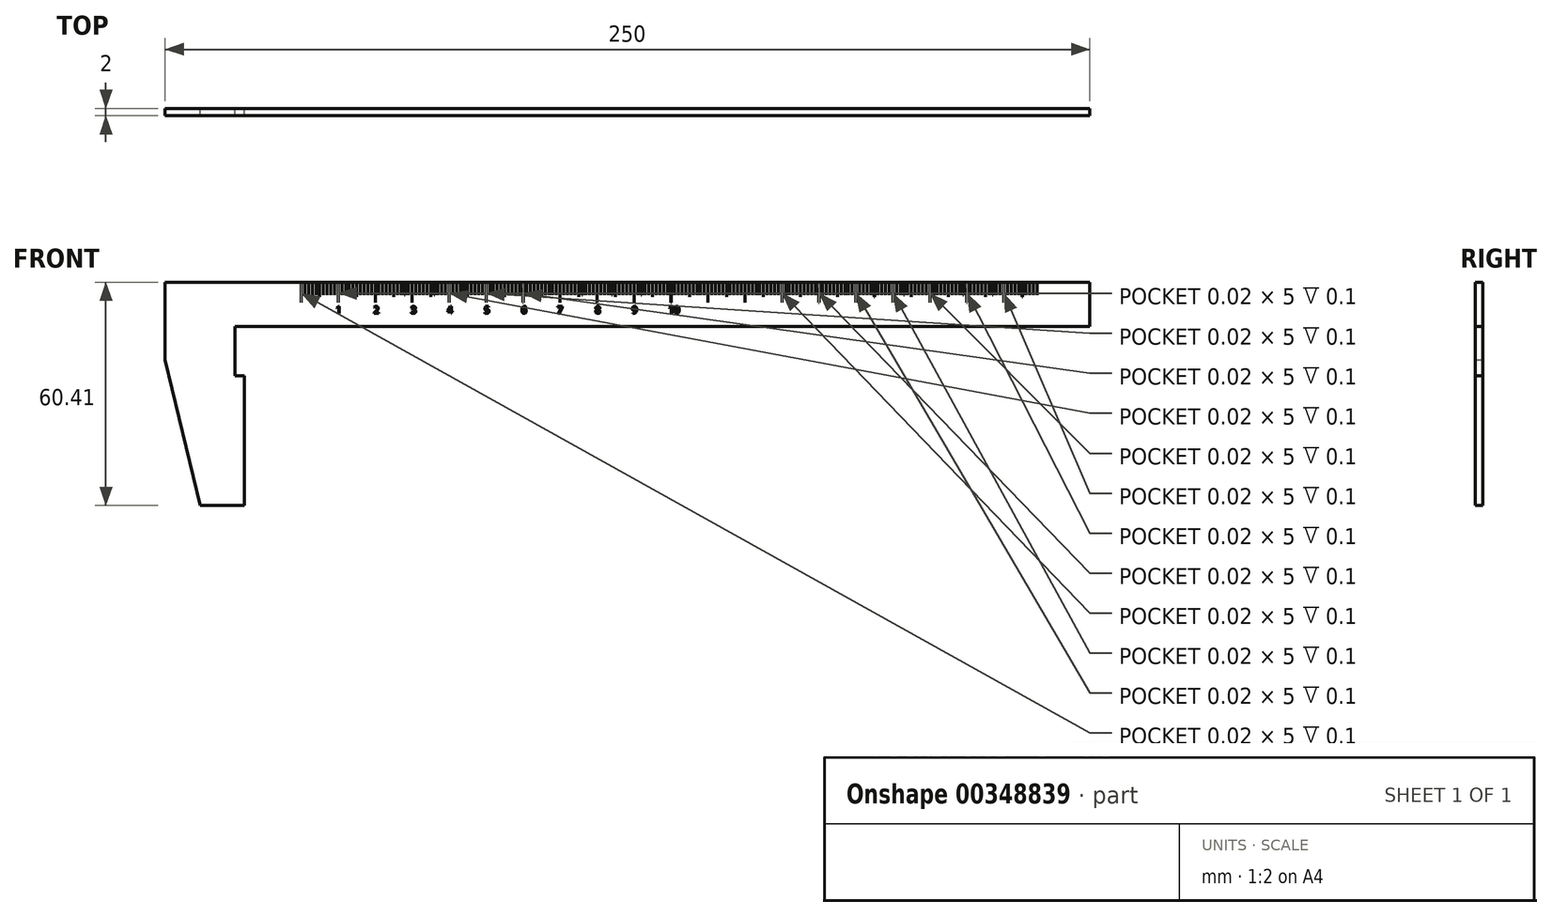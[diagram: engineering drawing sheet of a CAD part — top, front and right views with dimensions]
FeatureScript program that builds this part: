
annotation { "Feature Type Name" : "Feature", "Feature Type Description" : "" }
export const myFeature = defineFeature(function(context is Context, id is Id, definition is map)
    precondition{}
    {
        {
            var Q0;
            Q0=qCreatedBy(makeId("Front.planeOp"),FACE);
            var sketch = newSketch(context, id + "F0", { "sketchPlane" : qUnion([Q0])});
            skLineSegment(sketch, "E0.bottom", {"start": v(-86.98, 12) * mm, "end": v(123.02, 12) * mm});
            skLineSegment(sketch, "E0.top", {"start": v(-86.98, 0) * mm, "end": v(123.02, 0) * mm});
            skLineSegment(sketch, "E0.left", {"start": v(-86.98, 12) * mm, "end": v(-86.98, 0) * mm});
            skLineSegment(sketch, "E0.right", {"start": v(123.02, 12) * mm, "end": v(123.02, 0) * mm});
            skLineSegment(sketch, "E1", {"start": v(-86.98, 12) * mm, "end": v(-126.98, 12) * mm});
            skLineSegment(sketch, "E2", {"start": v(-126.98, 12) * mm, "end": v(-126.98, -9.03) * mm});
            skLineSegment(sketch, "E3", {"start": v(-126.98, -9.03) * mm, "end": v(-117.52, -48.4) * mm});
            skLineSegment(sketch, "E4", {"start": v(-105.6, -48.4) * mm, "end": v(-105.6, -13.34) * mm});
            skLineSegment(sketch, "E5", {"start": v(-105.6, 0) * mm, "end": v(-86.98, 0) * mm});
            skLineSegment(sketch, "E6", {"start": v(-117.52, -48.4) * mm, "end": v(-105.6, -48.4) * mm});
            skLineSegment(sketch, "E7", {"start": v(-105.6, -13.34) * mm, "end": v(-108.05, -13.33) * mm});
            skLineSegment(sketch, "E8", {"start": v(-108.05, -13.33) * mm, "end": v(-108.05, 0) * mm});
            skLineSegment(sketch, "E9", {"start": v(-108.05, 0) * mm, "end": v(-105.6, 0) * mm});
            skSolve(sketch);
        }
        {
            var Q0;
            Q0 = qSketchRegion(id + "F0", true);
            extrude(context, id + "F1", {"entities" : qUnion([Q0]), "depth" : 2 * mm});
        }
        {
            var Q0;
            Q0=makeQuery(id+"F1.opExtrude","CAP_FACE",FACE,{"disambiguationData":[OSD([sQuery(id+"F0.wireOp",EDGE,"E0.bottom"),sQuery(id+"F0.wireOp",EDGE,"E0.top"),sQuery(id+"F0.wireOp",EDGE,"E0.left"),sQuery(id+"F0.wireOp",EDGE,"E0.right")])],"isStart":false});
            var sketch = newSketch(context, id + "F2", { "sketchPlane" : qUnion([Q0])});
            skLineSegment(sketch, "E10.bottom", {"start": v(-90.2, 11.5) * mm, "end": v(-90.18, 11.5) * mm});
            skLineSegment(sketch, "E10.top", {"start": v(-90.2, 6.5) * mm, "end": v(-90.18, 6.5) * mm});
            skLineSegment(sketch, "E10.left", {"start": v(-90.2, 11.5) * mm, "end": v(-90.2, 6.5) * mm});
            skLineSegment(sketch, "E10.right", {"start": v(-90.18, 11.5) * mm, "end": v(-90.18, 6.5) * mm});
            skLineSegment(sketch, "E11.bottom", {"start": v(-89.2, 11.5) * mm, "end": v(-89.19, 11.5) * mm});
            skLineSegment(sketch, "E11.top", {"start": v(-89.2, 8.5) * mm, "end": v(-89.19, 8.5) * mm});
            skLineSegment(sketch, "E11.left", {"start": v(-89.2, 11.5) * mm, "end": v(-89.2, 8.5) * mm});
            skLineSegment(sketch, "E11.right", {"start": v(-89.19, 11.5) * mm, "end": v(-89.19, 8.5) * mm});
            skLineSegment(sketch, "E12.1.0.0", {"start": v(-88.2, 11.5) * mm, "end": v(-88.2, 8.5) * mm});
            skLineSegment(sketch, "E12.1.0.1", {"start": v(-88.19, 11.5) * mm, "end": v(-88.19, 8.5) * mm});
            skLineSegment(sketch, "E12.1.0.2", {"start": v(-88.2, 11.5) * mm, "end": v(-88.19, 11.5) * mm});
            skLineSegment(sketch, "E12.1.0.3", {"start": v(-88.2, 8.5) * mm, "end": v(-88.19, 8.5) * mm});
            skLineSegment(sketch, "E12.2.0.0", {"start": v(-87.2, 11.5) * mm, "end": v(-87.2, 8.5) * mm});
            skLineSegment(sketch, "E12.2.0.1", {"start": v(-87.19, 11.5) * mm, "end": v(-87.19, 8.5) * mm});
            skLineSegment(sketch, "E12.2.0.2", {"start": v(-87.2, 11.5) * mm, "end": v(-87.19, 11.5) * mm});
            skLineSegment(sketch, "E12.2.0.3", {"start": v(-87.2, 8.5) * mm, "end": v(-87.19, 8.5) * mm});
            skLineSegment(sketch, "E12.3.0.0", {"start": v(-86.2, 11.5) * mm, "end": v(-86.2, 8.5) * mm});
            skLineSegment(sketch, "E12.3.0.1", {"start": v(-86.19, 11.5) * mm, "end": v(-86.19, 8.5) * mm});
            skLineSegment(sketch, "E12.3.0.2", {"start": v(-86.2, 11.5) * mm, "end": v(-86.19, 11.5) * mm});
            skLineSegment(sketch, "E12.3.0.3", {"start": v(-86.2, 8.5) * mm, "end": v(-86.19, 8.5) * mm});
            skLineSegment(sketch, "E12.5.0.0", {"start": v(-84.2, 11.5) * mm, "end": v(-84.2, 8.5) * mm});
            skLineSegment(sketch, "E12.5.0.1", {"start": v(-84.19, 11.5) * mm, "end": v(-84.19, 8.5) * mm});
            skLineSegment(sketch, "E12.5.0.2", {"start": v(-84.2, 11.5) * mm, "end": v(-84.19, 11.5) * mm});
            skLineSegment(sketch, "E12.5.0.3", {"start": v(-84.2, 8.5) * mm, "end": v(-84.19, 8.5) * mm});
            skLineSegment(sketch, "E12.6.0.0", {"start": v(-83.2, 11.5) * mm, "end": v(-83.2, 8.5) * mm});
            skLineSegment(sketch, "E12.6.0.1", {"start": v(-83.19, 11.5) * mm, "end": v(-83.19, 8.5) * mm});
            skLineSegment(sketch, "E12.6.0.2", {"start": v(-83.2, 11.5) * mm, "end": v(-83.19, 11.5) * mm});
            skLineSegment(sketch, "E12.6.0.3", {"start": v(-83.2, 8.5) * mm, "end": v(-83.19, 8.5) * mm});
            skLineSegment(sketch, "E12.7.0.0", {"start": v(-82.2, 11.5) * mm, "end": v(-82.2, 8.5) * mm});
            skLineSegment(sketch, "E12.7.0.1", {"start": v(-82.19, 11.5) * mm, "end": v(-82.19, 8.5) * mm});
            skLineSegment(sketch, "E12.7.0.2", {"start": v(-82.2, 11.5) * mm, "end": v(-82.19, 11.5) * mm});
            skLineSegment(sketch, "E12.7.0.3", {"start": v(-82.2, 8.5) * mm, "end": v(-82.19, 8.5) * mm});
            skLineSegment(sketch, "E12.8.0.0", {"start": v(-81.2, 11.5) * mm, "end": v(-81.2, 8.5) * mm});
            skLineSegment(sketch, "E12.8.0.1", {"start": v(-81.19, 11.5) * mm, "end": v(-81.19, 8.5) * mm});
            skLineSegment(sketch, "E12.8.0.2", {"start": v(-81.2, 11.5) * mm, "end": v(-81.19, 11.5) * mm});
            skLineSegment(sketch, "E12.8.0.3", {"start": v(-81.2, 8.5) * mm, "end": v(-81.19, 8.5) * mm});
            skLineSegment(sketch, "E12.direction1", {"start": v(-89.2, 8.5) * mm, "end": v(-88.2, 8.5) * mm, "construction": true});
            skLineSegment(sketch, "E13.bottom", {"start": v(-85.2, 11.5) * mm, "end": v(-85.19, 11.5) * mm});
            skLineSegment(sketch, "E13.top", {"start": v(-85.2, 8) * mm, "end": v(-85.19, 8) * mm});
            skLineSegment(sketch, "E13.left", {"start": v(-85.2, 11.5) * mm, "end": v(-85.2, 8) * mm});
            skLineSegment(sketch, "E13.right", {"start": v(-85.19, 11.5) * mm, "end": v(-85.19, 8) * mm});
            skLineSegment(sketch, "E14.1.0.0", {"start": v(-80.18, 11.5) * mm, "end": v(-80.18, 6.5) * mm});
            skLineSegment(sketch, "E14.1.0.1", {"start": v(-73.19, 11.5) * mm, "end": v(-73.19, 8.5) * mm});
            skLineSegment(sketch, "E14.1.0.2", {"start": v(-78.19, 11.5) * mm, "end": v(-78.19, 8.5) * mm});
            skLineSegment(sketch, "E14.1.0.3", {"start": v(-80.2, 11.5) * mm, "end": v(-80.2, 6.5) * mm});
            skLineSegment(sketch, "E14.1.0.4", {"start": v(-76.19, 11.5) * mm, "end": v(-76.19, 8.5) * mm});
            skLineSegment(sketch, "E14.1.0.5", {"start": v(-71.19, 11.5) * mm, "end": v(-71.19, 8.5) * mm});
            skLineSegment(sketch, "E14.1.0.6", {"start": v(-74.19, 11.5) * mm, "end": v(-74.19, 8.5) * mm});
            skLineSegment(sketch, "E14.1.0.7", {"start": v(-75.19, 11.5) * mm, "end": v(-75.19, 8) * mm});
            skLineSegment(sketch, "E14.1.0.8", {"start": v(-77.2, 11.5) * mm, "end": v(-77.2, 8.5) * mm});
            skLineSegment(sketch, "E14.1.0.9", {"start": v(-72.2, 11.5) * mm, "end": v(-72.2, 8.5) * mm});
            skLineSegment(sketch, "E14.1.0.10", {"start": v(-79.19, 11.5) * mm, "end": v(-79.19, 8.5) * mm});
            skLineSegment(sketch, "E14.1.0.11", {"start": v(-71.2, 11.5) * mm, "end": v(-71.2, 8.5) * mm});
            skLineSegment(sketch, "E14.1.0.12", {"start": v(-79.2, 8.5) * mm, "end": v(-78.2, 8.5) * mm, "construction": true});
            skLineSegment(sketch, "E14.1.0.13", {"start": v(-77.19, 11.5) * mm, "end": v(-77.19, 8.5) * mm});
            skLineSegment(sketch, "E14.1.0.14", {"start": v(-73.2, 11.5) * mm, "end": v(-73.2, 8.5) * mm});
            skLineSegment(sketch, "E14.1.0.15", {"start": v(-79.2, 11.5) * mm, "end": v(-79.2, 8.5) * mm});
            skLineSegment(sketch, "E14.1.0.16", {"start": v(-78.2, 11.5) * mm, "end": v(-78.2, 8.5) * mm});
            skLineSegment(sketch, "E14.1.0.17", {"start": v(-76.2, 11.5) * mm, "end": v(-76.2, 8.5) * mm});
            skLineSegment(sketch, "E14.1.0.18", {"start": v(-74.2, 11.5) * mm, "end": v(-74.2, 8.5) * mm});
            skLineSegment(sketch, "E14.1.0.19", {"start": v(-72.19, 11.5) * mm, "end": v(-72.19, 8.5) * mm});
            skLineSegment(sketch, "E14.1.0.20", {"start": v(-75.2, 11.5) * mm, "end": v(-75.2, 8) * mm});
            skLineSegment(sketch, "E14.1.0.21", {"start": v(-71.2, 8.5) * mm, "end": v(-71.19, 8.5) * mm});
            skLineSegment(sketch, "E14.1.0.22", {"start": v(-80.2, 11.5) * mm, "end": v(-80.18, 11.5) * mm});
            skLineSegment(sketch, "E14.1.0.23", {"start": v(-80.2, 6.5) * mm, "end": v(-80.18, 6.5) * mm});
            skLineSegment(sketch, "E14.1.0.24", {"start": v(-71.2, 11.5) * mm, "end": v(-71.19, 11.5) * mm});
            skLineSegment(sketch, "E14.1.0.25", {"start": v(-77.2, 11.5) * mm, "end": v(-77.19, 11.5) * mm});
            skLineSegment(sketch, "E14.1.0.26", {"start": v(-74.2, 11.5) * mm, "end": v(-74.19, 11.5) * mm});
            skLineSegment(sketch, "E14.1.0.27", {"start": v(-72.2, 8.5) * mm, "end": v(-72.19, 8.5) * mm});
            skLineSegment(sketch, "E14.1.0.28", {"start": v(-75.2, 8) * mm, "end": v(-75.19, 8) * mm});
            skLineSegment(sketch, "E14.1.0.29", {"start": v(-77.2, 8.5) * mm, "end": v(-77.19, 8.5) * mm});
            skLineSegment(sketch, "E14.1.0.30", {"start": v(-73.2, 11.5) * mm, "end": v(-73.19, 11.5) * mm});
            skLineSegment(sketch, "E14.1.0.31", {"start": v(-78.2, 11.5) * mm, "end": v(-78.19, 11.5) * mm});
            skLineSegment(sketch, "E14.1.0.32", {"start": v(-75.2, 11.5) * mm, "end": v(-75.19, 11.5) * mm});
            skLineSegment(sketch, "E14.1.0.33", {"start": v(-72.2, 11.5) * mm, "end": v(-72.19, 11.5) * mm});
            skLineSegment(sketch, "E14.1.0.34", {"start": v(-79.2, 11.5) * mm, "end": v(-79.19, 11.5) * mm});
            skLineSegment(sketch, "E14.1.0.35", {"start": v(-76.2, 11.5) * mm, "end": v(-76.19, 11.5) * mm});
            skLineSegment(sketch, "E14.1.0.36", {"start": v(-74.2, 8.5) * mm, "end": v(-74.19, 8.5) * mm});
            skLineSegment(sketch, "E14.1.0.37", {"start": v(-73.2, 8.5) * mm, "end": v(-73.19, 8.5) * mm});
            skLineSegment(sketch, "E14.1.0.38", {"start": v(-76.2, 8.5) * mm, "end": v(-76.19, 8.5) * mm});
            skLineSegment(sketch, "E14.1.0.39", {"start": v(-78.2, 8.5) * mm, "end": v(-78.19, 8.5) * mm});
            skLineSegment(sketch, "E14.1.0.40", {"start": v(-79.2, 8.5) * mm, "end": v(-79.19, 8.5) * mm});
            skLineSegment(sketch, "E14.2.0.0", {"start": v(-70.18, 11.5) * mm, "end": v(-70.18, 6.5) * mm});
            skLineSegment(sketch, "E14.2.0.1", {"start": v(-63.19, 11.5) * mm, "end": v(-63.19, 8.5) * mm});
            skLineSegment(sketch, "E14.2.0.2", {"start": v(-68.19, 11.5) * mm, "end": v(-68.19, 8.5) * mm});
            skLineSegment(sketch, "E14.2.0.3", {"start": v(-70.2, 11.5) * mm, "end": v(-70.2, 6.5) * mm});
            skLineSegment(sketch, "E14.2.0.4", {"start": v(-66.19, 11.5) * mm, "end": v(-66.19, 8.5) * mm});
            skLineSegment(sketch, "E14.2.0.5", {"start": v(-61.19, 11.5) * mm, "end": v(-61.19, 8.5) * mm});
            skLineSegment(sketch, "E14.2.0.6", {"start": v(-64.19, 11.5) * mm, "end": v(-64.19, 8.5) * mm});
            skLineSegment(sketch, "E14.2.0.7", {"start": v(-65.19, 11.5) * mm, "end": v(-65.19, 8) * mm});
            skLineSegment(sketch, "E14.2.0.8", {"start": v(-67.2, 11.5) * mm, "end": v(-67.2, 8.5) * mm});
            skLineSegment(sketch, "E14.2.0.9", {"start": v(-62.2, 11.5) * mm, "end": v(-62.2, 8.5) * mm});
            skLineSegment(sketch, "E14.2.0.10", {"start": v(-69.19, 11.5) * mm, "end": v(-69.19, 8.5) * mm});
            skLineSegment(sketch, "E14.2.0.11", {"start": v(-61.2, 11.5) * mm, "end": v(-61.2, 8.5) * mm});
            skLineSegment(sketch, "E14.2.0.12", {"start": v(-69.2, 8.5) * mm, "end": v(-68.2, 8.5) * mm, "construction": true});
            skLineSegment(sketch, "E14.2.0.13", {"start": v(-67.19, 11.5) * mm, "end": v(-67.19, 8.5) * mm});
            skLineSegment(sketch, "E14.2.0.14", {"start": v(-63.2, 11.5) * mm, "end": v(-63.2, 8.5) * mm});
            skLineSegment(sketch, "E14.2.0.15", {"start": v(-69.2, 11.5) * mm, "end": v(-69.2, 8.5) * mm});
            skLineSegment(sketch, "E14.2.0.16", {"start": v(-68.2, 11.5) * mm, "end": v(-68.2, 8.5) * mm});
            skLineSegment(sketch, "E14.2.0.17", {"start": v(-66.2, 11.5) * mm, "end": v(-66.2, 8.5) * mm});
            skLineSegment(sketch, "E14.2.0.18", {"start": v(-64.2, 11.5) * mm, "end": v(-64.2, 8.5) * mm});
            skLineSegment(sketch, "E14.2.0.19", {"start": v(-62.19, 11.5) * mm, "end": v(-62.19, 8.5) * mm});
            skLineSegment(sketch, "E14.2.0.20", {"start": v(-65.2, 11.5) * mm, "end": v(-65.2, 8) * mm});
            skLineSegment(sketch, "E14.2.0.21", {"start": v(-61.2, 8.5) * mm, "end": v(-61.19, 8.5) * mm});
            skLineSegment(sketch, "E14.2.0.22", {"start": v(-70.2, 11.5) * mm, "end": v(-70.18, 11.5) * mm});
            skLineSegment(sketch, "E14.2.0.23", {"start": v(-70.2, 6.5) * mm, "end": v(-70.18, 6.5) * mm});
            skLineSegment(sketch, "E14.2.0.24", {"start": v(-61.2, 11.5) * mm, "end": v(-61.19, 11.5) * mm});
            skLineSegment(sketch, "E14.2.0.25", {"start": v(-67.2, 11.5) * mm, "end": v(-67.19, 11.5) * mm});
            skLineSegment(sketch, "E14.2.0.26", {"start": v(-64.2, 11.5) * mm, "end": v(-64.19, 11.5) * mm});
            skLineSegment(sketch, "E14.2.0.27", {"start": v(-62.2, 8.5) * mm, "end": v(-62.19, 8.5) * mm});
            skLineSegment(sketch, "E14.2.0.28", {"start": v(-65.2, 8) * mm, "end": v(-65.19, 8) * mm});
            skLineSegment(sketch, "E14.2.0.29", {"start": v(-67.2, 8.5) * mm, "end": v(-67.19, 8.5) * mm});
            skLineSegment(sketch, "E14.2.0.30", {"start": v(-63.2, 11.5) * mm, "end": v(-63.19, 11.5) * mm});
            skLineSegment(sketch, "E14.2.0.31", {"start": v(-68.2, 11.5) * mm, "end": v(-68.19, 11.5) * mm});
            skLineSegment(sketch, "E14.2.0.32", {"start": v(-65.2, 11.5) * mm, "end": v(-65.19, 11.5) * mm});
            skLineSegment(sketch, "E14.2.0.33", {"start": v(-62.2, 11.5) * mm, "end": v(-62.19, 11.5) * mm});
            skLineSegment(sketch, "E14.2.0.34", {"start": v(-69.2, 11.5) * mm, "end": v(-69.19, 11.5) * mm});
            skLineSegment(sketch, "E14.2.0.35", {"start": v(-66.2, 11.5) * mm, "end": v(-66.19, 11.5) * mm});
            skLineSegment(sketch, "E14.2.0.36", {"start": v(-64.2, 8.5) * mm, "end": v(-64.19, 8.5) * mm});
            skLineSegment(sketch, "E14.2.0.37", {"start": v(-63.2, 8.5) * mm, "end": v(-63.19, 8.5) * mm});
            skLineSegment(sketch, "E14.2.0.38", {"start": v(-66.2, 8.5) * mm, "end": v(-66.19, 8.5) * mm});
            skLineSegment(sketch, "E14.2.0.39", {"start": v(-68.2, 8.5) * mm, "end": v(-68.19, 8.5) * mm});
            skLineSegment(sketch, "E14.2.0.40", {"start": v(-69.2, 8.5) * mm, "end": v(-69.19, 8.5) * mm});
            skLineSegment(sketch, "E14.3.0.0", {"start": v(-60.18, 11.5) * mm, "end": v(-60.18, 6.5) * mm});
            skLineSegment(sketch, "E14.3.0.1", {"start": v(-53.19, 11.5) * mm, "end": v(-53.19, 8.5) * mm});
            skLineSegment(sketch, "E14.3.0.2", {"start": v(-58.19, 11.5) * mm, "end": v(-58.19, 8.5) * mm});
            skLineSegment(sketch, "E14.3.0.3", {"start": v(-60.2, 11.5) * mm, "end": v(-60.2, 6.5) * mm});
            skLineSegment(sketch, "E14.3.0.4", {"start": v(-56.19, 11.5) * mm, "end": v(-56.19, 8.5) * mm});
            skLineSegment(sketch, "E14.3.0.5", {"start": v(-51.19, 11.5) * mm, "end": v(-51.19, 8.5) * mm});
            skLineSegment(sketch, "E14.3.0.6", {"start": v(-54.19, 11.5) * mm, "end": v(-54.19, 8.5) * mm});
            skLineSegment(sketch, "E14.3.0.7", {"start": v(-55.19, 11.5) * mm, "end": v(-55.19, 8) * mm});
            skLineSegment(sketch, "E14.3.0.8", {"start": v(-57.2, 11.5) * mm, "end": v(-57.2, 8.5) * mm});
            skLineSegment(sketch, "E14.3.0.9", {"start": v(-52.2, 11.5) * mm, "end": v(-52.2, 8.5) * mm});
            skLineSegment(sketch, "E14.3.0.10", {"start": v(-59.19, 11.5) * mm, "end": v(-59.19, 8.5) * mm});
            skLineSegment(sketch, "E14.3.0.11", {"start": v(-51.2, 11.5) * mm, "end": v(-51.2, 8.5) * mm});
            skLineSegment(sketch, "E14.3.0.12", {"start": v(-59.2, 8.5) * mm, "end": v(-58.2, 8.5) * mm, "construction": true});
            skLineSegment(sketch, "E14.3.0.13", {"start": v(-57.19, 11.5) * mm, "end": v(-57.19, 8.5) * mm});
            skLineSegment(sketch, "E14.3.0.14", {"start": v(-53.2, 11.5) * mm, "end": v(-53.2, 8.5) * mm});
            skLineSegment(sketch, "E14.3.0.15", {"start": v(-59.2, 11.5) * mm, "end": v(-59.2, 8.5) * mm});
            skLineSegment(sketch, "E14.3.0.16", {"start": v(-58.2, 11.5) * mm, "end": v(-58.2, 8.5) * mm});
            skLineSegment(sketch, "E14.3.0.17", {"start": v(-56.2, 11.5) * mm, "end": v(-56.2, 8.5) * mm});
            skLineSegment(sketch, "E14.3.0.18", {"start": v(-54.2, 11.5) * mm, "end": v(-54.2, 8.5) * mm});
            skLineSegment(sketch, "E14.3.0.19", {"start": v(-52.19, 11.5) * mm, "end": v(-52.19, 8.5) * mm});
            skLineSegment(sketch, "E14.3.0.20", {"start": v(-55.2, 11.5) * mm, "end": v(-55.2, 8) * mm});
            skLineSegment(sketch, "E14.3.0.21", {"start": v(-51.2, 8.5) * mm, "end": v(-51.19, 8.5) * mm});
            skLineSegment(sketch, "E14.3.0.22", {"start": v(-60.2, 11.5) * mm, "end": v(-60.18, 11.5) * mm});
            skLineSegment(sketch, "E14.3.0.23", {"start": v(-60.2, 6.5) * mm, "end": v(-60.18, 6.5) * mm});
            skLineSegment(sketch, "E14.3.0.24", {"start": v(-51.2, 11.5) * mm, "end": v(-51.19, 11.5) * mm});
            skLineSegment(sketch, "E14.3.0.25", {"start": v(-57.2, 11.5) * mm, "end": v(-57.19, 11.5) * mm});
            skLineSegment(sketch, "E14.3.0.26", {"start": v(-54.2, 11.5) * mm, "end": v(-54.19, 11.5) * mm});
            skLineSegment(sketch, "E14.3.0.27", {"start": v(-52.2, 8.5) * mm, "end": v(-52.19, 8.5) * mm});
            skLineSegment(sketch, "E14.3.0.28", {"start": v(-55.2, 8) * mm, "end": v(-55.19, 8) * mm});
            skLineSegment(sketch, "E14.3.0.29", {"start": v(-57.2, 8.5) * mm, "end": v(-57.19, 8.5) * mm});
            skLineSegment(sketch, "E14.3.0.30", {"start": v(-53.2, 11.5) * mm, "end": v(-53.19, 11.5) * mm});
            skLineSegment(sketch, "E14.3.0.31", {"start": v(-58.2, 11.5) * mm, "end": v(-58.19, 11.5) * mm});
            skLineSegment(sketch, "E14.3.0.32", {"start": v(-55.2, 11.5) * mm, "end": v(-55.19, 11.5) * mm});
            skLineSegment(sketch, "E14.3.0.33", {"start": v(-52.2, 11.5) * mm, "end": v(-52.19, 11.5) * mm});
            skLineSegment(sketch, "E14.3.0.34", {"start": v(-59.2, 11.5) * mm, "end": v(-59.19, 11.5) * mm});
            skLineSegment(sketch, "E14.3.0.35", {"start": v(-56.2, 11.5) * mm, "end": v(-56.19, 11.5) * mm});
            skLineSegment(sketch, "E14.3.0.36", {"start": v(-54.2, 8.5) * mm, "end": v(-54.19, 8.5) * mm});
            skLineSegment(sketch, "E14.3.0.37", {"start": v(-53.2, 8.5) * mm, "end": v(-53.19, 8.5) * mm});
            skLineSegment(sketch, "E14.3.0.38", {"start": v(-56.2, 8.5) * mm, "end": v(-56.19, 8.5) * mm});
            skLineSegment(sketch, "E14.3.0.39", {"start": v(-58.2, 8.5) * mm, "end": v(-58.19, 8.5) * mm});
            skLineSegment(sketch, "E14.3.0.40", {"start": v(-59.2, 8.5) * mm, "end": v(-59.19, 8.5) * mm});
            skLineSegment(sketch, "E14.4.0.0", {"start": v(-50.18, 11.5) * mm, "end": v(-50.18, 6.5) * mm});
            skLineSegment(sketch, "E14.4.0.1", {"start": v(-43.19, 11.5) * mm, "end": v(-43.19, 8.5) * mm});
            skLineSegment(sketch, "E14.4.0.2", {"start": v(-48.19, 11.5) * mm, "end": v(-48.19, 8.5) * mm});
            skLineSegment(sketch, "E14.4.0.3", {"start": v(-50.2, 11.5) * mm, "end": v(-50.2, 6.5) * mm});
            skLineSegment(sketch, "E14.4.0.4", {"start": v(-46.19, 11.5) * mm, "end": v(-46.19, 8.5) * mm});
            skLineSegment(sketch, "E14.4.0.5", {"start": v(-41.19, 11.5) * mm, "end": v(-41.19, 8.5) * mm});
            skLineSegment(sketch, "E14.4.0.6", {"start": v(-44.19, 11.5) * mm, "end": v(-44.19, 8.5) * mm});
            skLineSegment(sketch, "E14.4.0.7", {"start": v(-45.19, 11.5) * mm, "end": v(-45.19, 8) * mm});
            skLineSegment(sketch, "E14.4.0.8", {"start": v(-47.2, 11.5) * mm, "end": v(-47.2, 8.5) * mm});
            skLineSegment(sketch, "E14.4.0.9", {"start": v(-42.2, 11.5) * mm, "end": v(-42.2, 8.5) * mm});
            skLineSegment(sketch, "E14.4.0.10", {"start": v(-49.19, 11.5) * mm, "end": v(-49.19, 8.5) * mm});
            skLineSegment(sketch, "E14.4.0.11", {"start": v(-41.2, 11.5) * mm, "end": v(-41.2, 8.5) * mm});
            skLineSegment(sketch, "E14.4.0.12", {"start": v(-49.2, 8.5) * mm, "end": v(-48.2, 8.5) * mm, "construction": true});
            skLineSegment(sketch, "E14.4.0.13", {"start": v(-47.19, 11.5) * mm, "end": v(-47.19, 8.5) * mm});
            skLineSegment(sketch, "E14.4.0.14", {"start": v(-43.2, 11.5) * mm, "end": v(-43.2, 8.5) * mm});
            skLineSegment(sketch, "E14.4.0.15", {"start": v(-49.2, 11.5) * mm, "end": v(-49.2, 8.5) * mm});
            skLineSegment(sketch, "E14.4.0.16", {"start": v(-48.2, 11.5) * mm, "end": v(-48.2, 8.5) * mm});
            skLineSegment(sketch, "E14.4.0.17", {"start": v(-46.2, 11.5) * mm, "end": v(-46.2, 8.5) * mm});
            skLineSegment(sketch, "E14.4.0.18", {"start": v(-44.2, 11.5) * mm, "end": v(-44.2, 8.5) * mm});
            skLineSegment(sketch, "E14.4.0.19", {"start": v(-42.19, 11.5) * mm, "end": v(-42.19, 8.5) * mm});
            skLineSegment(sketch, "E14.4.0.20", {"start": v(-45.2, 11.5) * mm, "end": v(-45.2, 8) * mm});
            skLineSegment(sketch, "E14.4.0.21", {"start": v(-41.2, 8.5) * mm, "end": v(-41.19, 8.5) * mm});
            skLineSegment(sketch, "E14.4.0.22", {"start": v(-50.2, 11.5) * mm, "end": v(-50.18, 11.5) * mm});
            skLineSegment(sketch, "E14.4.0.23", {"start": v(-50.2, 6.5) * mm, "end": v(-50.18, 6.5) * mm});
            skLineSegment(sketch, "E14.4.0.24", {"start": v(-41.2, 11.5) * mm, "end": v(-41.19, 11.5) * mm});
            skLineSegment(sketch, "E14.4.0.25", {"start": v(-47.2, 11.5) * mm, "end": v(-47.19, 11.5) * mm});
            skLineSegment(sketch, "E14.4.0.26", {"start": v(-44.2, 11.5) * mm, "end": v(-44.19, 11.5) * mm});
            skLineSegment(sketch, "E14.4.0.27", {"start": v(-42.2, 8.5) * mm, "end": v(-42.19, 8.5) * mm});
            skLineSegment(sketch, "E14.4.0.28", {"start": v(-45.2, 8) * mm, "end": v(-45.19, 8) * mm});
            skLineSegment(sketch, "E14.4.0.29", {"start": v(-47.2, 8.5) * mm, "end": v(-47.19, 8.5) * mm});
            skLineSegment(sketch, "E14.4.0.30", {"start": v(-43.2, 11.5) * mm, "end": v(-43.19, 11.5) * mm});
            skLineSegment(sketch, "E14.4.0.31", {"start": v(-48.2, 11.5) * mm, "end": v(-48.19, 11.5) * mm});
            skLineSegment(sketch, "E14.4.0.32", {"start": v(-45.2, 11.5) * mm, "end": v(-45.19, 11.5) * mm});
            skLineSegment(sketch, "E14.4.0.33", {"start": v(-42.2, 11.5) * mm, "end": v(-42.19, 11.5) * mm});
            skLineSegment(sketch, "E14.4.0.34", {"start": v(-49.2, 11.5) * mm, "end": v(-49.19, 11.5) * mm});
            skLineSegment(sketch, "E14.4.0.35", {"start": v(-46.2, 11.5) * mm, "end": v(-46.19, 11.5) * mm});
            skLineSegment(sketch, "E14.4.0.36", {"start": v(-44.2, 8.5) * mm, "end": v(-44.19, 8.5) * mm});
            skLineSegment(sketch, "E14.4.0.37", {"start": v(-43.2, 8.5) * mm, "end": v(-43.19, 8.5) * mm});
            skLineSegment(sketch, "E14.4.0.38", {"start": v(-46.2, 8.5) * mm, "end": v(-46.19, 8.5) * mm});
            skLineSegment(sketch, "E14.4.0.39", {"start": v(-48.2, 8.5) * mm, "end": v(-48.19, 8.5) * mm});
            skLineSegment(sketch, "E14.4.0.40", {"start": v(-49.2, 8.5) * mm, "end": v(-49.19, 8.5) * mm});
            skLineSegment(sketch, "E14.5.0.0", {"start": v(-40.18, 11.5) * mm, "end": v(-40.18, 6.5) * mm});
            skLineSegment(sketch, "E14.5.0.1", {"start": v(-33.19, 11.5) * mm, "end": v(-33.19, 8.5) * mm});
            skLineSegment(sketch, "E14.5.0.2", {"start": v(-38.19, 11.5) * mm, "end": v(-38.19, 8.5) * mm});
            skLineSegment(sketch, "E14.5.0.3", {"start": v(-40.2, 11.5) * mm, "end": v(-40.2, 6.5) * mm});
            skLineSegment(sketch, "E14.5.0.4", {"start": v(-36.19, 11.5) * mm, "end": v(-36.19, 8.5) * mm});
            skLineSegment(sketch, "E14.5.0.5", {"start": v(-31.19, 11.5) * mm, "end": v(-31.19, 8.5) * mm});
            skLineSegment(sketch, "E14.5.0.6", {"start": v(-34.19, 11.5) * mm, "end": v(-34.19, 8.5) * mm});
            skLineSegment(sketch, "E14.5.0.7", {"start": v(-35.19, 11.5) * mm, "end": v(-35.19, 8) * mm});
            skLineSegment(sketch, "E14.5.0.8", {"start": v(-37.2, 11.5) * mm, "end": v(-37.2, 8.5) * mm});
            skLineSegment(sketch, "E14.5.0.9", {"start": v(-32.2, 11.5) * mm, "end": v(-32.2, 8.5) * mm});
            skLineSegment(sketch, "E14.5.0.10", {"start": v(-39.19, 11.5) * mm, "end": v(-39.19, 8.5) * mm});
            skLineSegment(sketch, "E14.5.0.11", {"start": v(-31.2, 11.5) * mm, "end": v(-31.2, 8.5) * mm});
            skLineSegment(sketch, "E14.5.0.12", {"start": v(-39.2, 8.5) * mm, "end": v(-38.2, 8.5) * mm, "construction": true});
            skLineSegment(sketch, "E14.5.0.13", {"start": v(-37.19, 11.5) * mm, "end": v(-37.19, 8.5) * mm});
            skLineSegment(sketch, "E14.5.0.14", {"start": v(-33.2, 11.5) * mm, "end": v(-33.2, 8.5) * mm});
            skLineSegment(sketch, "E14.5.0.15", {"start": v(-39.2, 11.5) * mm, "end": v(-39.2, 8.5) * mm});
            skLineSegment(sketch, "E14.5.0.16", {"start": v(-38.2, 11.5) * mm, "end": v(-38.2, 8.5) * mm});
            skLineSegment(sketch, "E14.5.0.17", {"start": v(-36.2, 11.5) * mm, "end": v(-36.2, 8.5) * mm});
            skLineSegment(sketch, "E14.5.0.18", {"start": v(-34.2, 11.5) * mm, "end": v(-34.2, 8.5) * mm});
            skLineSegment(sketch, "E14.5.0.19", {"start": v(-32.19, 11.5) * mm, "end": v(-32.19, 8.5) * mm});
            skLineSegment(sketch, "E14.5.0.20", {"start": v(-35.2, 11.5) * mm, "end": v(-35.2, 8) * mm});
            skLineSegment(sketch, "E14.5.0.21", {"start": v(-31.2, 8.5) * mm, "end": v(-31.19, 8.5) * mm});
            skLineSegment(sketch, "E14.5.0.22", {"start": v(-40.2, 11.5) * mm, "end": v(-40.18, 11.5) * mm});
            skLineSegment(sketch, "E14.5.0.23", {"start": v(-40.2, 6.5) * mm, "end": v(-40.18, 6.5) * mm});
            skLineSegment(sketch, "E14.5.0.24", {"start": v(-31.2, 11.5) * mm, "end": v(-31.19, 11.5) * mm});
            skLineSegment(sketch, "E14.5.0.25", {"start": v(-37.2, 11.5) * mm, "end": v(-37.19, 11.5) * mm});
            skLineSegment(sketch, "E14.5.0.26", {"start": v(-34.2, 11.5) * mm, "end": v(-34.19, 11.5) * mm});
            skLineSegment(sketch, "E14.5.0.27", {"start": v(-32.2, 8.5) * mm, "end": v(-32.19, 8.5) * mm});
            skLineSegment(sketch, "E14.5.0.28", {"start": v(-35.2, 8) * mm, "end": v(-35.19, 8) * mm});
            skLineSegment(sketch, "E14.5.0.29", {"start": v(-37.2, 8.5) * mm, "end": v(-37.19, 8.5) * mm});
            skLineSegment(sketch, "E14.5.0.30", {"start": v(-33.2, 11.5) * mm, "end": v(-33.19, 11.5) * mm});
            skLineSegment(sketch, "E14.5.0.31", {"start": v(-38.2, 11.5) * mm, "end": v(-38.19, 11.5) * mm});
            skLineSegment(sketch, "E14.5.0.32", {"start": v(-35.2, 11.5) * mm, "end": v(-35.19, 11.5) * mm});
            skLineSegment(sketch, "E14.5.0.33", {"start": v(-32.2, 11.5) * mm, "end": v(-32.19, 11.5) * mm});
            skLineSegment(sketch, "E14.5.0.34", {"start": v(-39.2, 11.5) * mm, "end": v(-39.19, 11.5) * mm});
            skLineSegment(sketch, "E14.5.0.35", {"start": v(-36.2, 11.5) * mm, "end": v(-36.19, 11.5) * mm});
            skLineSegment(sketch, "E14.5.0.36", {"start": v(-34.2, 8.5) * mm, "end": v(-34.19, 8.5) * mm});
            skLineSegment(sketch, "E14.5.0.37", {"start": v(-33.2, 8.5) * mm, "end": v(-33.19, 8.5) * mm});
            skLineSegment(sketch, "E14.5.0.38", {"start": v(-36.2, 8.5) * mm, "end": v(-36.19, 8.5) * mm});
            skLineSegment(sketch, "E14.5.0.39", {"start": v(-38.2, 8.5) * mm, "end": v(-38.19, 8.5) * mm});
            skLineSegment(sketch, "E14.5.0.40", {"start": v(-39.2, 8.5) * mm, "end": v(-39.19, 8.5) * mm});
            skLineSegment(sketch, "E14.6.0.0", {"start": v(-30.18, 11.5) * mm, "end": v(-30.18, 6.5) * mm});
            skLineSegment(sketch, "E14.6.0.1", {"start": v(-23.19, 11.5) * mm, "end": v(-23.19, 8.5) * mm});
            skLineSegment(sketch, "E14.6.0.2", {"start": v(-28.19, 11.5) * mm, "end": v(-28.19, 8.5) * mm});
            skLineSegment(sketch, "E14.6.0.3", {"start": v(-30.2, 11.5) * mm, "end": v(-30.2, 6.5) * mm});
            skLineSegment(sketch, "E14.6.0.4", {"start": v(-26.19, 11.5) * mm, "end": v(-26.19, 8.5) * mm});
            skLineSegment(sketch, "E14.6.0.5", {"start": v(-21.19, 11.5) * mm, "end": v(-21.19, 8.5) * mm});
            skLineSegment(sketch, "E14.6.0.6", {"start": v(-24.19, 11.5) * mm, "end": v(-24.19, 8.5) * mm});
            skLineSegment(sketch, "E14.6.0.7", {"start": v(-25.19, 11.5) * mm, "end": v(-25.19, 8) * mm});
            skLineSegment(sketch, "E14.6.0.8", {"start": v(-27.2, 11.5) * mm, "end": v(-27.2, 8.5) * mm});
            skLineSegment(sketch, "E14.6.0.9", {"start": v(-22.2, 11.5) * mm, "end": v(-22.2, 8.5) * mm});
            skLineSegment(sketch, "E14.6.0.10", {"start": v(-29.19, 11.5) * mm, "end": v(-29.19, 8.5) * mm});
            skLineSegment(sketch, "E14.6.0.11", {"start": v(-21.2, 11.5) * mm, "end": v(-21.2, 8.5) * mm});
            skLineSegment(sketch, "E14.6.0.12", {"start": v(-29.2, 8.5) * mm, "end": v(-28.2, 8.5) * mm, "construction": true});
            skLineSegment(sketch, "E14.6.0.13", {"start": v(-27.19, 11.5) * mm, "end": v(-27.19, 8.5) * mm});
            skLineSegment(sketch, "E14.6.0.14", {"start": v(-23.2, 11.5) * mm, "end": v(-23.2, 8.5) * mm});
            skLineSegment(sketch, "E14.6.0.15", {"start": v(-29.2, 11.5) * mm, "end": v(-29.2, 8.5) * mm});
            skLineSegment(sketch, "E14.6.0.16", {"start": v(-28.2, 11.5) * mm, "end": v(-28.2, 8.5) * mm});
            skLineSegment(sketch, "E14.6.0.17", {"start": v(-26.2, 11.5) * mm, "end": v(-26.2, 8.5) * mm});
            skLineSegment(sketch, "E14.6.0.18", {"start": v(-24.2, 11.5) * mm, "end": v(-24.2, 8.5) * mm});
            skLineSegment(sketch, "E14.6.0.19", {"start": v(-22.19, 11.5) * mm, "end": v(-22.19, 8.5) * mm});
            skLineSegment(sketch, "E14.6.0.20", {"start": v(-25.2, 11.5) * mm, "end": v(-25.2, 8) * mm});
            skLineSegment(sketch, "E14.6.0.21", {"start": v(-21.2, 8.5) * mm, "end": v(-21.19, 8.5) * mm});
            skLineSegment(sketch, "E14.6.0.22", {"start": v(-30.2, 11.5) * mm, "end": v(-30.18, 11.5) * mm});
            skLineSegment(sketch, "E14.6.0.23", {"start": v(-30.2, 6.5) * mm, "end": v(-30.18, 6.5) * mm});
            skLineSegment(sketch, "E14.6.0.24", {"start": v(-21.2, 11.5) * mm, "end": v(-21.19, 11.5) * mm});
            skLineSegment(sketch, "E14.6.0.25", {"start": v(-27.2, 11.5) * mm, "end": v(-27.19, 11.5) * mm});
            skLineSegment(sketch, "E14.6.0.26", {"start": v(-24.2, 11.5) * mm, "end": v(-24.19, 11.5) * mm});
            skLineSegment(sketch, "E14.6.0.27", {"start": v(-22.2, 8.5) * mm, "end": v(-22.19, 8.5) * mm});
            skLineSegment(sketch, "E14.6.0.28", {"start": v(-25.2, 8) * mm, "end": v(-25.19, 8) * mm});
            skLineSegment(sketch, "E14.6.0.29", {"start": v(-27.2, 8.5) * mm, "end": v(-27.19, 8.5) * mm});
            skLineSegment(sketch, "E14.6.0.30", {"start": v(-23.2, 11.5) * mm, "end": v(-23.19, 11.5) * mm});
            skLineSegment(sketch, "E14.6.0.31", {"start": v(-28.2, 11.5) * mm, "end": v(-28.19, 11.5) * mm});
            skLineSegment(sketch, "E14.6.0.32", {"start": v(-25.2, 11.5) * mm, "end": v(-25.19, 11.5) * mm});
            skLineSegment(sketch, "E14.6.0.33", {"start": v(-22.2, 11.5) * mm, "end": v(-22.19, 11.5) * mm});
            skLineSegment(sketch, "E14.6.0.34", {"start": v(-29.2, 11.5) * mm, "end": v(-29.19, 11.5) * mm});
            skLineSegment(sketch, "E14.6.0.35", {"start": v(-26.2, 11.5) * mm, "end": v(-26.19, 11.5) * mm});
            skLineSegment(sketch, "E14.6.0.36", {"start": v(-24.2, 8.5) * mm, "end": v(-24.19, 8.5) * mm});
            skLineSegment(sketch, "E14.6.0.37", {"start": v(-23.2, 8.5) * mm, "end": v(-23.19, 8.5) * mm});
            skLineSegment(sketch, "E14.6.0.38", {"start": v(-26.2, 8.5) * mm, "end": v(-26.19, 8.5) * mm});
            skLineSegment(sketch, "E14.6.0.39", {"start": v(-28.2, 8.5) * mm, "end": v(-28.19, 8.5) * mm});
            skLineSegment(sketch, "E14.6.0.40", {"start": v(-29.2, 8.5) * mm, "end": v(-29.19, 8.5) * mm});
            skLineSegment(sketch, "E14.7.0.0", {"start": v(-20.18, 11.5) * mm, "end": v(-20.18, 6.5) * mm});
            skLineSegment(sketch, "E14.7.0.1", {"start": v(-13.19, 11.5) * mm, "end": v(-13.19, 8.5) * mm});
            skLineSegment(sketch, "E14.7.0.2", {"start": v(-18.19, 11.5) * mm, "end": v(-18.19, 8.5) * mm});
            skLineSegment(sketch, "E14.7.0.3", {"start": v(-20.2, 11.5) * mm, "end": v(-20.2, 6.5) * mm});
            skLineSegment(sketch, "E14.7.0.4", {"start": v(-16.19, 11.5) * mm, "end": v(-16.19, 8.5) * mm});
            skLineSegment(sketch, "E14.7.0.5", {"start": v(-11.19, 11.5) * mm, "end": v(-11.19, 8.5) * mm});
            skLineSegment(sketch, "E14.7.0.6", {"start": v(-14.19, 11.5) * mm, "end": v(-14.19, 8.5) * mm});
            skLineSegment(sketch, "E14.7.0.7", {"start": v(-15.19, 11.5) * mm, "end": v(-15.19, 8) * mm});
            skLineSegment(sketch, "E14.7.0.8", {"start": v(-17.2, 11.5) * mm, "end": v(-17.2, 8.5) * mm});
            skLineSegment(sketch, "E14.7.0.9", {"start": v(-12.2, 11.5) * mm, "end": v(-12.2, 8.5) * mm});
            skLineSegment(sketch, "E14.7.0.10", {"start": v(-19.19, 11.5) * mm, "end": v(-19.19, 8.5) * mm});
            skLineSegment(sketch, "E14.7.0.11", {"start": v(-11.2, 11.5) * mm, "end": v(-11.2, 8.5) * mm});
            skLineSegment(sketch, "E14.7.0.12", {"start": v(-19.2, 8.5) * mm, "end": v(-18.2, 8.5) * mm, "construction": true});
            skLineSegment(sketch, "E14.7.0.13", {"start": v(-17.19, 11.5) * mm, "end": v(-17.19, 8.5) * mm});
            skLineSegment(sketch, "E14.7.0.14", {"start": v(-13.2, 11.5) * mm, "end": v(-13.2, 8.5) * mm});
            skLineSegment(sketch, "E14.7.0.15", {"start": v(-19.2, 11.5) * mm, "end": v(-19.2, 8.5) * mm});
            skLineSegment(sketch, "E14.7.0.16", {"start": v(-18.2, 11.5) * mm, "end": v(-18.2, 8.5) * mm});
            skLineSegment(sketch, "E14.7.0.17", {"start": v(-16.2, 11.5) * mm, "end": v(-16.2, 8.5) * mm});
            skLineSegment(sketch, "E14.7.0.18", {"start": v(-14.2, 11.5) * mm, "end": v(-14.2, 8.5) * mm});
            skLineSegment(sketch, "E14.7.0.19", {"start": v(-12.19, 11.5) * mm, "end": v(-12.19, 8.5) * mm});
            skLineSegment(sketch, "E14.7.0.20", {"start": v(-15.2, 11.5) * mm, "end": v(-15.2, 8) * mm});
            skLineSegment(sketch, "E14.7.0.21", {"start": v(-11.2, 8.5) * mm, "end": v(-11.19, 8.5) * mm});
            skLineSegment(sketch, "E14.7.0.22", {"start": v(-20.2, 11.5) * mm, "end": v(-20.18, 11.5) * mm});
            skLineSegment(sketch, "E14.7.0.23", {"start": v(-20.2, 6.5) * mm, "end": v(-20.18, 6.5) * mm});
            skLineSegment(sketch, "E14.7.0.24", {"start": v(-11.2, 11.5) * mm, "end": v(-11.19, 11.5) * mm});
            skLineSegment(sketch, "E14.7.0.25", {"start": v(-17.2, 11.5) * mm, "end": v(-17.19, 11.5) * mm});
            skLineSegment(sketch, "E14.7.0.26", {"start": v(-14.2, 11.5) * mm, "end": v(-14.19, 11.5) * mm});
            skLineSegment(sketch, "E14.7.0.27", {"start": v(-12.2, 8.5) * mm, "end": v(-12.19, 8.5) * mm});
            skLineSegment(sketch, "E14.7.0.28", {"start": v(-15.2, 8) * mm, "end": v(-15.19, 8) * mm});
            skLineSegment(sketch, "E14.7.0.29", {"start": v(-17.2, 8.5) * mm, "end": v(-17.19, 8.5) * mm});
            skLineSegment(sketch, "E14.7.0.30", {"start": v(-13.2, 11.5) * mm, "end": v(-13.19, 11.5) * mm});
            skLineSegment(sketch, "E14.7.0.31", {"start": v(-18.2, 11.5) * mm, "end": v(-18.19, 11.5) * mm});
            skLineSegment(sketch, "E14.7.0.32", {"start": v(-15.2, 11.5) * mm, "end": v(-15.19, 11.5) * mm});
            skLineSegment(sketch, "E14.7.0.33", {"start": v(-12.2, 11.5) * mm, "end": v(-12.19, 11.5) * mm});
            skLineSegment(sketch, "E14.7.0.34", {"start": v(-19.2, 11.5) * mm, "end": v(-19.19, 11.5) * mm});
            skLineSegment(sketch, "E14.7.0.35", {"start": v(-16.2, 11.5) * mm, "end": v(-16.19, 11.5) * mm});
            skLineSegment(sketch, "E14.7.0.36", {"start": v(-14.2, 8.5) * mm, "end": v(-14.19, 8.5) * mm});
            skLineSegment(sketch, "E14.7.0.37", {"start": v(-13.2, 8.5) * mm, "end": v(-13.19, 8.5) * mm});
            skLineSegment(sketch, "E14.7.0.38", {"start": v(-16.2, 8.5) * mm, "end": v(-16.19, 8.5) * mm});
            skLineSegment(sketch, "E14.7.0.39", {"start": v(-18.2, 8.5) * mm, "end": v(-18.19, 8.5) * mm});
            skLineSegment(sketch, "E14.7.0.40", {"start": v(-19.2, 8.5) * mm, "end": v(-19.19, 8.5) * mm});
            skLineSegment(sketch, "E14.8.0.0", {"start": v(-10.18, 11.5) * mm, "end": v(-10.18, 6.5) * mm});
            skLineSegment(sketch, "E14.8.0.1", {"start": v(-3.19, 11.5) * mm, "end": v(-3.19, 8.5) * mm});
            skLineSegment(sketch, "E14.8.0.2", {"start": v(-8.19, 11.5) * mm, "end": v(-8.19, 8.5) * mm});
            skLineSegment(sketch, "E14.8.0.3", {"start": v(-10.2, 11.5) * mm, "end": v(-10.2, 6.5) * mm});
            skLineSegment(sketch, "E14.8.0.4", {"start": v(-6.19, 11.5) * mm, "end": v(-6.19, 8.5) * mm});
            skLineSegment(sketch, "E14.8.0.5", {"start": v(-1.19, 11.5) * mm, "end": v(-1.19, 8.5) * mm});
            skLineSegment(sketch, "E14.8.0.6", {"start": v(-4.19, 11.5) * mm, "end": v(-4.19, 8.5) * mm});
            skLineSegment(sketch, "E14.8.0.7", {"start": v(-5.19, 11.5) * mm, "end": v(-5.19, 8) * mm});
            skLineSegment(sketch, "E14.8.0.8", {"start": v(-7.2, 11.5) * mm, "end": v(-7.2, 8.5) * mm});
            skLineSegment(sketch, "E14.8.0.9", {"start": v(-2.2, 11.5) * mm, "end": v(-2.2, 8.5) * mm});
            skLineSegment(sketch, "E14.8.0.10", {"start": v(-9.19, 11.5) * mm, "end": v(-9.19, 8.5) * mm});
            skLineSegment(sketch, "E14.8.0.11", {"start": v(-1.2, 11.5) * mm, "end": v(-1.2, 8.5) * mm});
            skLineSegment(sketch, "E14.8.0.12", {"start": v(-9.2, 8.5) * mm, "end": v(-8.2, 8.5) * mm, "construction": true});
            skLineSegment(sketch, "E14.8.0.13", {"start": v(-7.19, 11.5) * mm, "end": v(-7.19, 8.5) * mm});
            skLineSegment(sketch, "E14.8.0.14", {"start": v(-3.2, 11.5) * mm, "end": v(-3.2, 8.5) * mm});
            skLineSegment(sketch, "E14.8.0.15", {"start": v(-9.2, 11.5) * mm, "end": v(-9.2, 8.5) * mm});
            skLineSegment(sketch, "E14.8.0.16", {"start": v(-8.2, 11.5) * mm, "end": v(-8.2, 8.5) * mm});
            skLineSegment(sketch, "E14.8.0.17", {"start": v(-6.2, 11.5) * mm, "end": v(-6.2, 8.5) * mm});
            skLineSegment(sketch, "E14.8.0.18", {"start": v(-4.2, 11.5) * mm, "end": v(-4.2, 8.5) * mm});
            skLineSegment(sketch, "E14.8.0.19", {"start": v(-2.19, 11.5) * mm, "end": v(-2.19, 8.5) * mm});
            skLineSegment(sketch, "E14.8.0.20", {"start": v(-5.2, 11.5) * mm, "end": v(-5.2, 8) * mm});
            skLineSegment(sketch, "E14.8.0.21", {"start": v(-1.2, 8.5) * mm, "end": v(-1.19, 8.5) * mm});
            skLineSegment(sketch, "E14.8.0.22", {"start": v(-10.2, 11.5) * mm, "end": v(-10.18, 11.5) * mm});
            skLineSegment(sketch, "E14.8.0.23", {"start": v(-10.2, 6.5) * mm, "end": v(-10.18, 6.5) * mm});
            skLineSegment(sketch, "E14.8.0.24", {"start": v(-1.2, 11.5) * mm, "end": v(-1.19, 11.5) * mm});
            skLineSegment(sketch, "E14.8.0.25", {"start": v(-7.2, 11.5) * mm, "end": v(-7.19, 11.5) * mm});
            skLineSegment(sketch, "E14.8.0.26", {"start": v(-4.2, 11.5) * mm, "end": v(-4.19, 11.5) * mm});
            skLineSegment(sketch, "E14.8.0.27", {"start": v(-2.2, 8.5) * mm, "end": v(-2.19, 8.5) * mm});
            skLineSegment(sketch, "E14.8.0.28", {"start": v(-5.2, 8) * mm, "end": v(-5.19, 8) * mm});
            skLineSegment(sketch, "E14.8.0.29", {"start": v(-7.2, 8.5) * mm, "end": v(-7.19, 8.5) * mm});
            skLineSegment(sketch, "E14.8.0.30", {"start": v(-3.2, 11.5) * mm, "end": v(-3.19, 11.5) * mm});
            skLineSegment(sketch, "E14.8.0.31", {"start": v(-8.2, 11.5) * mm, "end": v(-8.19, 11.5) * mm});
            skLineSegment(sketch, "E14.8.0.32", {"start": v(-5.2, 11.5) * mm, "end": v(-5.19, 11.5) * mm});
            skLineSegment(sketch, "E14.8.0.33", {"start": v(-2.2, 11.5) * mm, "end": v(-2.19, 11.5) * mm});
            skLineSegment(sketch, "E14.8.0.34", {"start": v(-9.2, 11.5) * mm, "end": v(-9.19, 11.5) * mm});
            skLineSegment(sketch, "E14.8.0.35", {"start": v(-6.2, 11.5) * mm, "end": v(-6.19, 11.5) * mm});
            skLineSegment(sketch, "E14.8.0.36", {"start": v(-4.2, 8.5) * mm, "end": v(-4.19, 8.5) * mm});
            skLineSegment(sketch, "E14.8.0.37", {"start": v(-3.2, 8.5) * mm, "end": v(-3.19, 8.5) * mm});
            skLineSegment(sketch, "E14.8.0.38", {"start": v(-6.2, 8.5) * mm, "end": v(-6.19, 8.5) * mm});
            skLineSegment(sketch, "E14.8.0.39", {"start": v(-8.2, 8.5) * mm, "end": v(-8.19, 8.5) * mm});
            skLineSegment(sketch, "E14.8.0.40", {"start": v(-9.2, 8.5) * mm, "end": v(-9.19, 8.5) * mm});
            skLineSegment(sketch, "E14.9.0.0", {"start": v(-0.18, 11.5) * mm, "end": v(-0.18, 6.5) * mm});
            skLineSegment(sketch, "E14.9.0.1", {"start": v(6.81, 11.5) * mm, "end": v(6.81, 8.5) * mm});
            skLineSegment(sketch, "E14.9.0.2", {"start": v(1.81, 11.5) * mm, "end": v(1.81, 8.5) * mm});
            skLineSegment(sketch, "E14.9.0.3", {"start": v(-0.2, 11.5) * mm, "end": v(-0.2, 6.5) * mm});
            skLineSegment(sketch, "E14.9.0.4", {"start": v(3.81, 11.5) * mm, "end": v(3.81, 8.5) * mm});
            skLineSegment(sketch, "E14.9.0.5", {"start": v(8.81, 11.5) * mm, "end": v(8.81, 8.5) * mm});
            skLineSegment(sketch, "E14.9.0.6", {"start": v(5.81, 11.5) * mm, "end": v(5.81, 8.5) * mm});
            skLineSegment(sketch, "E14.9.0.7", {"start": v(4.81, 11.5) * mm, "end": v(4.81, 8) * mm});
            skLineSegment(sketch, "E14.9.0.8", {"start": v(2.8, 11.5) * mm, "end": v(2.8, 8.5) * mm});
            skLineSegment(sketch, "E14.9.0.9", {"start": v(7.8, 11.5) * mm, "end": v(7.8, 8.5) * mm});
            skLineSegment(sketch, "E14.9.0.10", {"start": v(0.81, 11.5) * mm, "end": v(0.81, 8.5) * mm});
            skLineSegment(sketch, "E14.9.0.11", {"start": v(8.8, 11.5) * mm, "end": v(8.8, 8.5) * mm});
            skLineSegment(sketch, "E14.9.0.12", {"start": v(0.8, 8.5) * mm, "end": v(1.8, 8.5) * mm, "construction": true});
            skLineSegment(sketch, "E14.9.0.13", {"start": v(2.81, 11.5) * mm, "end": v(2.81, 8.5) * mm});
            skLineSegment(sketch, "E14.9.0.14", {"start": v(6.8, 11.5) * mm, "end": v(6.8, 8.5) * mm});
            skLineSegment(sketch, "E14.9.0.15", {"start": v(0.8, 11.5) * mm, "end": v(0.8, 8.5) * mm});
            skLineSegment(sketch, "E14.9.0.16", {"start": v(1.8, 11.5) * mm, "end": v(1.8, 8.5) * mm});
            skLineSegment(sketch, "E14.9.0.17", {"start": v(3.8, 11.5) * mm, "end": v(3.8, 8.5) * mm});
            skLineSegment(sketch, "E14.9.0.18", {"start": v(5.8, 11.5) * mm, "end": v(5.8, 8.5) * mm});
            skLineSegment(sketch, "E14.9.0.19", {"start": v(7.81, 11.5) * mm, "end": v(7.81, 8.5) * mm});
            skLineSegment(sketch, "E14.9.0.20", {"start": v(4.8, 11.5) * mm, "end": v(4.8, 8) * mm});
            skLineSegment(sketch, "E14.9.0.21", {"start": v(8.8, 8.5) * mm, "end": v(8.81, 8.5) * mm});
            skLineSegment(sketch, "E14.9.0.22", {"start": v(-0.2, 11.5) * mm, "end": v(-0.18, 11.5) * mm});
            skLineSegment(sketch, "E14.9.0.23", {"start": v(-0.2, 6.5) * mm, "end": v(-0.18, 6.5) * mm});
            skLineSegment(sketch, "E14.9.0.24", {"start": v(8.8, 11.5) * mm, "end": v(8.81, 11.5) * mm});
            skLineSegment(sketch, "E14.9.0.25", {"start": v(2.8, 11.5) * mm, "end": v(2.81, 11.5) * mm});
            skLineSegment(sketch, "E14.9.0.26", {"start": v(5.8, 11.5) * mm, "end": v(5.81, 11.5) * mm});
            skLineSegment(sketch, "E14.9.0.27", {"start": v(7.8, 8.5) * mm, "end": v(7.81, 8.5) * mm});
            skLineSegment(sketch, "E14.9.0.28", {"start": v(4.8, 8) * mm, "end": v(4.81, 8) * mm});
            skLineSegment(sketch, "E14.9.0.29", {"start": v(2.8, 8.5) * mm, "end": v(2.81, 8.5) * mm});
            skLineSegment(sketch, "E14.9.0.30", {"start": v(6.8, 11.5) * mm, "end": v(6.81, 11.5) * mm});
            skLineSegment(sketch, "E14.9.0.31", {"start": v(1.8, 11.5) * mm, "end": v(1.81, 11.5) * mm});
            skLineSegment(sketch, "E14.9.0.32", {"start": v(4.8, 11.5) * mm, "end": v(4.81, 11.5) * mm});
            skLineSegment(sketch, "E14.9.0.33", {"start": v(7.8, 11.5) * mm, "end": v(7.81, 11.5) * mm});
            skLineSegment(sketch, "E14.9.0.34", {"start": v(0.8, 11.5) * mm, "end": v(0.81, 11.5) * mm});
            skLineSegment(sketch, "E14.9.0.35", {"start": v(3.8, 11.5) * mm, "end": v(3.81, 11.5) * mm});
            skLineSegment(sketch, "E14.9.0.36", {"start": v(5.8, 8.5) * mm, "end": v(5.81, 8.5) * mm});
            skLineSegment(sketch, "E14.9.0.37", {"start": v(6.8, 8.5) * mm, "end": v(6.81, 8.5) * mm});
            skLineSegment(sketch, "E14.9.0.38", {"start": v(3.8, 8.5) * mm, "end": v(3.81, 8.5) * mm});
            skLineSegment(sketch, "E14.9.0.39", {"start": v(1.8, 8.5) * mm, "end": v(1.81, 8.5) * mm});
            skLineSegment(sketch, "E14.9.0.40", {"start": v(0.8, 8.5) * mm, "end": v(0.81, 8.5) * mm});
            skLineSegment(sketch, "E14.10.0.0", {"start": v(9.82, 11.5) * mm, "end": v(9.82, 6.5) * mm});
            skLineSegment(sketch, "E14.10.0.1", {"start": v(16.81, 11.5) * mm, "end": v(16.81, 8.5) * mm});
            skLineSegment(sketch, "E14.10.0.2", {"start": v(11.81, 11.5) * mm, "end": v(11.81, 8.5) * mm});
            skLineSegment(sketch, "E14.10.0.3", {"start": v(9.8, 11.5) * mm, "end": v(9.8, 6.5) * mm});
            skLineSegment(sketch, "E14.10.0.4", {"start": v(13.81, 11.5) * mm, "end": v(13.81, 8.5) * mm});
            skLineSegment(sketch, "E14.10.0.5", {"start": v(18.81, 11.5) * mm, "end": v(18.81, 8.5) * mm});
            skLineSegment(sketch, "E14.10.0.6", {"start": v(15.81, 11.5) * mm, "end": v(15.81, 8.5) * mm});
            skLineSegment(sketch, "E14.10.0.7", {"start": v(14.81, 11.5) * mm, "end": v(14.81, 8) * mm});
            skLineSegment(sketch, "E14.10.0.8", {"start": v(12.8, 11.5) * mm, "end": v(12.8, 8.5) * mm});
            skLineSegment(sketch, "E14.10.0.9", {"start": v(17.8, 11.5) * mm, "end": v(17.8, 8.5) * mm});
            skLineSegment(sketch, "E14.10.0.10", {"start": v(10.81, 11.5) * mm, "end": v(10.81, 8.5) * mm});
            skLineSegment(sketch, "E14.10.0.11", {"start": v(18.8, 11.5) * mm, "end": v(18.8, 8.5) * mm});
            skLineSegment(sketch, "E14.10.0.12", {"start": v(10.8, 8.5) * mm, "end": v(11.8, 8.5) * mm, "construction": true});
            skLineSegment(sketch, "E14.10.0.13", {"start": v(12.81, 11.5) * mm, "end": v(12.81, 8.5) * mm});
            skLineSegment(sketch, "E14.10.0.14", {"start": v(16.8, 11.5) * mm, "end": v(16.8, 8.5) * mm});
            skLineSegment(sketch, "E14.10.0.15", {"start": v(10.8, 11.5) * mm, "end": v(10.8, 8.5) * mm});
            skLineSegment(sketch, "E14.10.0.16", {"start": v(11.8, 11.5) * mm, "end": v(11.8, 8.5) * mm});
            skLineSegment(sketch, "E14.10.0.17", {"start": v(13.8, 11.5) * mm, "end": v(13.8, 8.5) * mm});
            skLineSegment(sketch, "E14.10.0.18", {"start": v(15.8, 11.5) * mm, "end": v(15.8, 8.5) * mm});
            skLineSegment(sketch, "E14.10.0.19", {"start": v(17.81, 11.5) * mm, "end": v(17.81, 8.5) * mm});
            skLineSegment(sketch, "E14.10.0.20", {"start": v(14.8, 11.5) * mm, "end": v(14.8, 8) * mm});
            skLineSegment(sketch, "E14.10.0.21", {"start": v(18.8, 8.5) * mm, "end": v(18.81, 8.5) * mm});
            skLineSegment(sketch, "E14.10.0.22", {"start": v(9.8, 11.5) * mm, "end": v(9.82, 11.5) * mm});
            skLineSegment(sketch, "E14.10.0.23", {"start": v(9.8, 6.5) * mm, "end": v(9.82, 6.5) * mm});
            skLineSegment(sketch, "E14.10.0.24", {"start": v(18.8, 11.5) * mm, "end": v(18.81, 11.5) * mm});
            skLineSegment(sketch, "E14.10.0.25", {"start": v(12.8, 11.5) * mm, "end": v(12.81, 11.5) * mm});
            skLineSegment(sketch, "E14.10.0.26", {"start": v(15.8, 11.5) * mm, "end": v(15.81, 11.5) * mm});
            skLineSegment(sketch, "E14.10.0.27", {"start": v(17.8, 8.5) * mm, "end": v(17.81, 8.5) * mm});
            skLineSegment(sketch, "E14.10.0.28", {"start": v(14.8, 8) * mm, "end": v(14.81, 8) * mm});
            skLineSegment(sketch, "E14.10.0.29", {"start": v(12.8, 8.5) * mm, "end": v(12.81, 8.5) * mm});
            skLineSegment(sketch, "E14.10.0.30", {"start": v(16.8, 11.5) * mm, "end": v(16.81, 11.5) * mm});
            skLineSegment(sketch, "E14.10.0.31", {"start": v(11.8, 11.5) * mm, "end": v(11.81, 11.5) * mm});
            skLineSegment(sketch, "E14.10.0.32", {"start": v(14.8, 11.5) * mm, "end": v(14.81, 11.5) * mm});
            skLineSegment(sketch, "E14.10.0.33", {"start": v(17.8, 11.5) * mm, "end": v(17.81, 11.5) * mm});
            skLineSegment(sketch, "E14.10.0.34", {"start": v(10.8, 11.5) * mm, "end": v(10.81, 11.5) * mm});
            skLineSegment(sketch, "E14.10.0.35", {"start": v(13.8, 11.5) * mm, "end": v(13.81, 11.5) * mm});
            skLineSegment(sketch, "E14.10.0.36", {"start": v(15.8, 8.5) * mm, "end": v(15.81, 8.5) * mm});
            skLineSegment(sketch, "E14.10.0.37", {"start": v(16.8, 8.5) * mm, "end": v(16.81, 8.5) * mm});
            skLineSegment(sketch, "E14.10.0.38", {"start": v(13.8, 8.5) * mm, "end": v(13.81, 8.5) * mm});
            skLineSegment(sketch, "E14.10.0.39", {"start": v(11.8, 8.5) * mm, "end": v(11.81, 8.5) * mm});
            skLineSegment(sketch, "E14.10.0.40", {"start": v(10.8, 8.5) * mm, "end": v(10.81, 8.5) * mm});
            skLineSegment(sketch, "E14.11.0.0", {"start": v(19.82, 11.5) * mm, "end": v(19.82, 6.5) * mm});
            skLineSegment(sketch, "E14.11.0.1", {"start": v(26.81, 11.5) * mm, "end": v(26.81, 8.5) * mm});
            skLineSegment(sketch, "E14.11.0.2", {"start": v(21.81, 11.5) * mm, "end": v(21.81, 8.5) * mm});
            skLineSegment(sketch, "E14.11.0.3", {"start": v(19.8, 11.5) * mm, "end": v(19.8, 6.5) * mm});
            skLineSegment(sketch, "E14.11.0.4", {"start": v(23.81, 11.5) * mm, "end": v(23.81, 8.5) * mm});
            skLineSegment(sketch, "E14.11.0.5", {"start": v(28.81, 11.5) * mm, "end": v(28.81, 8.5) * mm});
            skLineSegment(sketch, "E14.11.0.6", {"start": v(25.81, 11.5) * mm, "end": v(25.81, 8.5) * mm});
            skLineSegment(sketch, "E14.11.0.7", {"start": v(24.81, 11.5) * mm, "end": v(24.81, 8) * mm});
            skLineSegment(sketch, "E14.11.0.8", {"start": v(22.8, 11.5) * mm, "end": v(22.8, 8.5) * mm});
            skLineSegment(sketch, "E14.11.0.9", {"start": v(27.8, 11.5) * mm, "end": v(27.8, 8.5) * mm});
            skLineSegment(sketch, "E14.11.0.10", {"start": v(20.81, 11.5) * mm, "end": v(20.81, 8.5) * mm});
            skLineSegment(sketch, "E14.11.0.11", {"start": v(28.8, 11.5) * mm, "end": v(28.8, 8.5) * mm});
            skLineSegment(sketch, "E14.11.0.12", {"start": v(20.8, 8.5) * mm, "end": v(21.8, 8.5) * mm, "construction": true});
            skLineSegment(sketch, "E14.11.0.13", {"start": v(22.81, 11.5) * mm, "end": v(22.81, 8.5) * mm});
            skLineSegment(sketch, "E14.11.0.14", {"start": v(26.8, 11.5) * mm, "end": v(26.8, 8.5) * mm});
            skLineSegment(sketch, "E14.11.0.15", {"start": v(20.8, 11.5) * mm, "end": v(20.8, 8.5) * mm});
            skLineSegment(sketch, "E14.11.0.16", {"start": v(21.8, 11.5) * mm, "end": v(21.8, 8.5) * mm});
            skLineSegment(sketch, "E14.11.0.17", {"start": v(23.8, 11.5) * mm, "end": v(23.8, 8.5) * mm});
            skLineSegment(sketch, "E14.11.0.18", {"start": v(25.8, 11.5) * mm, "end": v(25.8, 8.5) * mm});
            skLineSegment(sketch, "E14.11.0.19", {"start": v(27.81, 11.5) * mm, "end": v(27.81, 8.5) * mm});
            skLineSegment(sketch, "E14.11.0.20", {"start": v(24.8, 11.5) * mm, "end": v(24.8, 8) * mm});
            skLineSegment(sketch, "E14.11.0.21", {"start": v(28.8, 8.5) * mm, "end": v(28.81, 8.5) * mm});
            skLineSegment(sketch, "E14.11.0.22", {"start": v(19.8, 11.5) * mm, "end": v(19.82, 11.5) * mm});
            skLineSegment(sketch, "E14.11.0.23", {"start": v(19.8, 6.5) * mm, "end": v(19.82, 6.5) * mm});
            skLineSegment(sketch, "E14.11.0.24", {"start": v(28.8, 11.5) * mm, "end": v(28.81, 11.5) * mm});
            skLineSegment(sketch, "E14.11.0.25", {"start": v(22.8, 11.5) * mm, "end": v(22.81, 11.5) * mm});
            skLineSegment(sketch, "E14.11.0.26", {"start": v(25.8, 11.5) * mm, "end": v(25.81, 11.5) * mm});
            skLineSegment(sketch, "E14.11.0.27", {"start": v(27.8, 8.5) * mm, "end": v(27.81, 8.5) * mm});
            skLineSegment(sketch, "E14.11.0.28", {"start": v(24.8, 8) * mm, "end": v(24.81, 8) * mm});
            skLineSegment(sketch, "E14.11.0.29", {"start": v(22.8, 8.5) * mm, "end": v(22.81, 8.5) * mm});
            skLineSegment(sketch, "E14.11.0.30", {"start": v(26.8, 11.5) * mm, "end": v(26.81, 11.5) * mm});
            skLineSegment(sketch, "E14.11.0.31", {"start": v(21.8, 11.5) * mm, "end": v(21.81, 11.5) * mm});
            skLineSegment(sketch, "E14.11.0.32", {"start": v(24.8, 11.5) * mm, "end": v(24.81, 11.5) * mm});
            skLineSegment(sketch, "E14.11.0.33", {"start": v(27.8, 11.5) * mm, "end": v(27.81, 11.5) * mm});
            skLineSegment(sketch, "E14.11.0.34", {"start": v(20.8, 11.5) * mm, "end": v(20.81, 11.5) * mm});
            skLineSegment(sketch, "E14.11.0.35", {"start": v(23.8, 11.5) * mm, "end": v(23.81, 11.5) * mm});
            skLineSegment(sketch, "E14.11.0.36", {"start": v(25.8, 8.5) * mm, "end": v(25.81, 8.5) * mm});
            skLineSegment(sketch, "E14.11.0.37", {"start": v(26.8, 8.5) * mm, "end": v(26.81, 8.5) * mm});
            skLineSegment(sketch, "E14.11.0.38", {"start": v(23.8, 8.5) * mm, "end": v(23.81, 8.5) * mm});
            skLineSegment(sketch, "E14.11.0.39", {"start": v(21.8, 8.5) * mm, "end": v(21.81, 8.5) * mm});
            skLineSegment(sketch, "E14.11.0.40", {"start": v(20.8, 8.5) * mm, "end": v(20.81, 8.5) * mm});
            skLineSegment(sketch, "E14.12.0.0", {"start": v(29.82, 11.5) * mm, "end": v(29.82, 6.5) * mm});
            skLineSegment(sketch, "E14.12.0.1", {"start": v(36.81, 11.5) * mm, "end": v(36.81, 8.5) * mm});
            skLineSegment(sketch, "E14.12.0.2", {"start": v(31.81, 11.5) * mm, "end": v(31.81, 8.5) * mm});
            skLineSegment(sketch, "E14.12.0.3", {"start": v(29.8, 11.5) * mm, "end": v(29.8, 6.5) * mm});
            skLineSegment(sketch, "E14.12.0.4", {"start": v(33.81, 11.5) * mm, "end": v(33.81, 8.5) * mm});
            skLineSegment(sketch, "E14.12.0.5", {"start": v(38.81, 11.5) * mm, "end": v(38.81, 8.5) * mm});
            skLineSegment(sketch, "E14.12.0.6", {"start": v(35.81, 11.5) * mm, "end": v(35.81, 8.5) * mm});
            skLineSegment(sketch, "E14.12.0.7", {"start": v(34.81, 11.5) * mm, "end": v(34.81, 8) * mm});
            skLineSegment(sketch, "E14.12.0.8", {"start": v(32.8, 11.5) * mm, "end": v(32.8, 8.5) * mm});
            skLineSegment(sketch, "E14.12.0.9", {"start": v(37.8, 11.5) * mm, "end": v(37.8, 8.5) * mm});
            skLineSegment(sketch, "E14.12.0.10", {"start": v(30.81, 11.5) * mm, "end": v(30.81, 8.5) * mm});
            skLineSegment(sketch, "E14.12.0.11", {"start": v(38.8, 11.5) * mm, "end": v(38.8, 8.5) * mm});
            skLineSegment(sketch, "E14.12.0.12", {"start": v(30.8, 8.5) * mm, "end": v(31.8, 8.5) * mm, "construction": true});
            skLineSegment(sketch, "E14.12.0.13", {"start": v(32.81, 11.5) * mm, "end": v(32.81, 8.5) * mm});
            skLineSegment(sketch, "E14.12.0.14", {"start": v(36.8, 11.5) * mm, "end": v(36.8, 8.5) * mm});
            skLineSegment(sketch, "E14.12.0.15", {"start": v(30.8, 11.5) * mm, "end": v(30.8, 8.5) * mm});
            skLineSegment(sketch, "E14.12.0.16", {"start": v(31.8, 11.5) * mm, "end": v(31.8, 8.5) * mm});
            skLineSegment(sketch, "E14.12.0.17", {"start": v(33.8, 11.5) * mm, "end": v(33.8, 8.5) * mm});
            skLineSegment(sketch, "E14.12.0.18", {"start": v(35.8, 11.5) * mm, "end": v(35.8, 8.5) * mm});
            skLineSegment(sketch, "E14.12.0.19", {"start": v(37.81, 11.5) * mm, "end": v(37.81, 8.5) * mm});
            skLineSegment(sketch, "E14.12.0.20", {"start": v(34.8, 11.5) * mm, "end": v(34.8, 8) * mm});
            skLineSegment(sketch, "E14.12.0.21", {"start": v(38.8, 8.5) * mm, "end": v(38.81, 8.5) * mm});
            skLineSegment(sketch, "E14.12.0.22", {"start": v(29.8, 11.5) * mm, "end": v(29.82, 11.5) * mm});
            skLineSegment(sketch, "E14.12.0.23", {"start": v(29.8, 6.5) * mm, "end": v(29.82, 6.5) * mm});
            skLineSegment(sketch, "E14.12.0.24", {"start": v(38.8, 11.5) * mm, "end": v(38.81, 11.5) * mm});
            skLineSegment(sketch, "E14.12.0.25", {"start": v(32.8, 11.5) * mm, "end": v(32.81, 11.5) * mm});
            skLineSegment(sketch, "E14.12.0.26", {"start": v(35.8, 11.5) * mm, "end": v(35.81, 11.5) * mm});
            skLineSegment(sketch, "E14.12.0.27", {"start": v(37.8, 8.5) * mm, "end": v(37.81, 8.5) * mm});
            skLineSegment(sketch, "E14.12.0.28", {"start": v(34.8, 8) * mm, "end": v(34.81, 8) * mm});
            skLineSegment(sketch, "E14.12.0.29", {"start": v(32.8, 8.5) * mm, "end": v(32.81, 8.5) * mm});
            skLineSegment(sketch, "E14.12.0.30", {"start": v(36.8, 11.5) * mm, "end": v(36.81, 11.5) * mm});
            skLineSegment(sketch, "E14.12.0.31", {"start": v(31.8, 11.5) * mm, "end": v(31.81, 11.5) * mm});
            skLineSegment(sketch, "E14.12.0.32", {"start": v(34.8, 11.5) * mm, "end": v(34.81, 11.5) * mm});
            skLineSegment(sketch, "E14.12.0.33", {"start": v(37.8, 11.5) * mm, "end": v(37.81, 11.5) * mm});
            skLineSegment(sketch, "E14.12.0.34", {"start": v(30.8, 11.5) * mm, "end": v(30.81, 11.5) * mm});
            skLineSegment(sketch, "E14.12.0.35", {"start": v(33.8, 11.5) * mm, "end": v(33.81, 11.5) * mm});
            skLineSegment(sketch, "E14.12.0.36", {"start": v(35.8, 8.5) * mm, "end": v(35.81, 8.5) * mm});
            skLineSegment(sketch, "E14.12.0.37", {"start": v(36.8, 8.5) * mm, "end": v(36.81, 8.5) * mm});
            skLineSegment(sketch, "E14.12.0.38", {"start": v(33.8, 8.5) * mm, "end": v(33.81, 8.5) * mm});
            skLineSegment(sketch, "E14.12.0.39", {"start": v(31.8, 8.5) * mm, "end": v(31.81, 8.5) * mm});
            skLineSegment(sketch, "E14.12.0.40", {"start": v(30.8, 8.5) * mm, "end": v(30.81, 8.5) * mm});
            skLineSegment(sketch, "E14.13.0.0", {"start": v(39.82, 11.5) * mm, "end": v(39.82, 6.5) * mm});
            skLineSegment(sketch, "E14.13.0.1", {"start": v(46.81, 11.5) * mm, "end": v(46.81, 8.5) * mm});
            skLineSegment(sketch, "E14.13.0.2", {"start": v(41.81, 11.5) * mm, "end": v(41.81, 8.5) * mm});
            skLineSegment(sketch, "E14.13.0.3", {"start": v(39.8, 11.5) * mm, "end": v(39.8, 6.5) * mm});
            skLineSegment(sketch, "E14.13.0.4", {"start": v(43.81, 11.5) * mm, "end": v(43.81, 8.5) * mm});
            skLineSegment(sketch, "E14.13.0.5", {"start": v(48.81, 11.5) * mm, "end": v(48.81, 8.5) * mm});
            skLineSegment(sketch, "E14.13.0.6", {"start": v(45.81, 11.5) * mm, "end": v(45.81, 8.5) * mm});
            skLineSegment(sketch, "E14.13.0.7", {"start": v(44.81, 11.5) * mm, "end": v(44.81, 8) * mm});
            skLineSegment(sketch, "E14.13.0.8", {"start": v(42.8, 11.5) * mm, "end": v(42.8, 8.5) * mm});
            skLineSegment(sketch, "E14.13.0.9", {"start": v(47.8, 11.5) * mm, "end": v(47.8, 8.5) * mm});
            skLineSegment(sketch, "E14.13.0.10", {"start": v(40.81, 11.5) * mm, "end": v(40.81, 8.5) * mm});
            skLineSegment(sketch, "E14.13.0.11", {"start": v(48.8, 11.5) * mm, "end": v(48.8, 8.5) * mm});
            skLineSegment(sketch, "E14.13.0.12", {"start": v(40.8, 8.5) * mm, "end": v(41.8, 8.5) * mm, "construction": true});
            skLineSegment(sketch, "E14.13.0.13", {"start": v(42.81, 11.5) * mm, "end": v(42.81, 8.5) * mm});
            skLineSegment(sketch, "E14.13.0.14", {"start": v(46.8, 11.5) * mm, "end": v(46.8, 8.5) * mm});
            skLineSegment(sketch, "E14.13.0.15", {"start": v(40.8, 11.5) * mm, "end": v(40.8, 8.5) * mm});
            skLineSegment(sketch, "E14.13.0.16", {"start": v(41.8, 11.5) * mm, "end": v(41.8, 8.5) * mm});
            skLineSegment(sketch, "E14.13.0.17", {"start": v(43.8, 11.5) * mm, "end": v(43.8, 8.5) * mm});
            skLineSegment(sketch, "E14.13.0.18", {"start": v(45.8, 11.5) * mm, "end": v(45.8, 8.5) * mm});
            skLineSegment(sketch, "E14.13.0.19", {"start": v(47.81, 11.5) * mm, "end": v(47.81, 8.5) * mm});
            skLineSegment(sketch, "E14.13.0.20", {"start": v(44.8, 11.5) * mm, "end": v(44.8, 8) * mm});
            skLineSegment(sketch, "E14.13.0.21", {"start": v(48.8, 8.5) * mm, "end": v(48.81, 8.5) * mm});
            skLineSegment(sketch, "E14.13.0.22", {"start": v(39.8, 11.5) * mm, "end": v(39.82, 11.5) * mm});
            skLineSegment(sketch, "E14.13.0.23", {"start": v(39.8, 6.5) * mm, "end": v(39.82, 6.5) * mm});
            skLineSegment(sketch, "E14.13.0.24", {"start": v(48.8, 11.5) * mm, "end": v(48.81, 11.5) * mm});
            skLineSegment(sketch, "E14.13.0.25", {"start": v(42.8, 11.5) * mm, "end": v(42.81, 11.5) * mm});
            skLineSegment(sketch, "E14.13.0.26", {"start": v(45.8, 11.5) * mm, "end": v(45.81, 11.5) * mm});
            skLineSegment(sketch, "E14.13.0.27", {"start": v(47.8, 8.5) * mm, "end": v(47.81, 8.5) * mm});
            skLineSegment(sketch, "E14.13.0.28", {"start": v(44.8, 8) * mm, "end": v(44.81, 8) * mm});
            skLineSegment(sketch, "E14.13.0.29", {"start": v(42.8, 8.5) * mm, "end": v(42.81, 8.5) * mm});
            skLineSegment(sketch, "E14.13.0.30", {"start": v(46.8, 11.5) * mm, "end": v(46.81, 11.5) * mm});
            skLineSegment(sketch, "E14.13.0.31", {"start": v(41.8, 11.5) * mm, "end": v(41.81, 11.5) * mm});
            skLineSegment(sketch, "E14.13.0.32", {"start": v(44.8, 11.5) * mm, "end": v(44.81, 11.5) * mm});
            skLineSegment(sketch, "E14.13.0.33", {"start": v(47.8, 11.5) * mm, "end": v(47.81, 11.5) * mm});
            skLineSegment(sketch, "E14.13.0.34", {"start": v(40.8, 11.5) * mm, "end": v(40.81, 11.5) * mm});
            skLineSegment(sketch, "E14.13.0.35", {"start": v(43.8, 11.5) * mm, "end": v(43.81, 11.5) * mm});
            skLineSegment(sketch, "E14.13.0.36", {"start": v(45.8, 8.5) * mm, "end": v(45.81, 8.5) * mm});
            skLineSegment(sketch, "E14.13.0.37", {"start": v(46.8, 8.5) * mm, "end": v(46.81, 8.5) * mm});
            skLineSegment(sketch, "E14.13.0.38", {"start": v(43.8, 8.5) * mm, "end": v(43.81, 8.5) * mm});
            skLineSegment(sketch, "E14.13.0.39", {"start": v(41.8, 8.5) * mm, "end": v(41.81, 8.5) * mm});
            skLineSegment(sketch, "E14.13.0.40", {"start": v(40.8, 8.5) * mm, "end": v(40.81, 8.5) * mm});
            skLineSegment(sketch, "E14.14.0.0", {"start": v(49.82, 11.5) * mm, "end": v(49.82, 6.5) * mm});
            skLineSegment(sketch, "E14.14.0.1", {"start": v(56.81, 11.5) * mm, "end": v(56.81, 8.5) * mm});
            skLineSegment(sketch, "E14.14.0.2", {"start": v(51.81, 11.5) * mm, "end": v(51.81, 8.5) * mm});
            skLineSegment(sketch, "E14.14.0.3", {"start": v(49.8, 11.5) * mm, "end": v(49.8, 6.5) * mm});
            skLineSegment(sketch, "E14.14.0.4", {"start": v(53.81, 11.5) * mm, "end": v(53.81, 8.5) * mm});
            skLineSegment(sketch, "E14.14.0.5", {"start": v(58.81, 11.5) * mm, "end": v(58.81, 8.5) * mm});
            skLineSegment(sketch, "E14.14.0.6", {"start": v(55.81, 11.5) * mm, "end": v(55.81, 8.5) * mm});
            skLineSegment(sketch, "E14.14.0.7", {"start": v(54.81, 11.5) * mm, "end": v(54.81, 8) * mm});
            skLineSegment(sketch, "E14.14.0.8", {"start": v(52.8, 11.5) * mm, "end": v(52.8, 8.5) * mm});
            skLineSegment(sketch, "E14.14.0.9", {"start": v(57.8, 11.5) * mm, "end": v(57.8, 8.5) * mm});
            skLineSegment(sketch, "E14.14.0.10", {"start": v(50.81, 11.5) * mm, "end": v(50.81, 8.5) * mm});
            skLineSegment(sketch, "E14.14.0.11", {"start": v(58.8, 11.5) * mm, "end": v(58.8, 8.5) * mm});
            skLineSegment(sketch, "E14.14.0.12", {"start": v(50.8, 8.5) * mm, "end": v(51.8, 8.5) * mm, "construction": true});
            skLineSegment(sketch, "E14.14.0.13", {"start": v(52.81, 11.5) * mm, "end": v(52.81, 8.5) * mm});
            skLineSegment(sketch, "E14.14.0.14", {"start": v(56.8, 11.5) * mm, "end": v(56.8, 8.5) * mm});
            skLineSegment(sketch, "E14.14.0.15", {"start": v(50.8, 11.5) * mm, "end": v(50.8, 8.5) * mm});
            skLineSegment(sketch, "E14.14.0.16", {"start": v(51.8, 11.5) * mm, "end": v(51.8, 8.5) * mm});
            skLineSegment(sketch, "E14.14.0.17", {"start": v(53.8, 11.5) * mm, "end": v(53.8, 8.5) * mm});
            skLineSegment(sketch, "E14.14.0.18", {"start": v(55.8, 11.5) * mm, "end": v(55.8, 8.5) * mm});
            skLineSegment(sketch, "E14.14.0.19", {"start": v(57.81, 11.5) * mm, "end": v(57.81, 8.5) * mm});
            skLineSegment(sketch, "E14.14.0.20", {"start": v(54.8, 11.5) * mm, "end": v(54.8, 8) * mm});
            skLineSegment(sketch, "E14.14.0.21", {"start": v(58.8, 8.5) * mm, "end": v(58.81, 8.5) * mm});
            skLineSegment(sketch, "E14.14.0.22", {"start": v(49.8, 11.5) * mm, "end": v(49.82, 11.5) * mm});
            skLineSegment(sketch, "E14.14.0.23", {"start": v(49.8, 6.5) * mm, "end": v(49.82, 6.5) * mm});
            skLineSegment(sketch, "E14.14.0.24", {"start": v(58.8, 11.5) * mm, "end": v(58.81, 11.5) * mm});
            skLineSegment(sketch, "E14.14.0.25", {"start": v(52.8, 11.5) * mm, "end": v(52.81, 11.5) * mm});
            skLineSegment(sketch, "E14.14.0.26", {"start": v(55.8, 11.5) * mm, "end": v(55.81, 11.5) * mm});
            skLineSegment(sketch, "E14.14.0.27", {"start": v(57.8, 8.5) * mm, "end": v(57.81, 8.5) * mm});
            skLineSegment(sketch, "E14.14.0.28", {"start": v(54.8, 8) * mm, "end": v(54.81, 8) * mm});
            skLineSegment(sketch, "E14.14.0.29", {"start": v(52.8, 8.5) * mm, "end": v(52.81, 8.5) * mm});
            skLineSegment(sketch, "E14.14.0.30", {"start": v(56.8, 11.5) * mm, "end": v(56.81, 11.5) * mm});
            skLineSegment(sketch, "E14.14.0.31", {"start": v(51.8, 11.5) * mm, "end": v(51.81, 11.5) * mm});
            skLineSegment(sketch, "E14.14.0.32", {"start": v(54.8, 11.5) * mm, "end": v(54.81, 11.5) * mm});
            skLineSegment(sketch, "E14.14.0.33", {"start": v(57.8, 11.5) * mm, "end": v(57.81, 11.5) * mm});
            skLineSegment(sketch, "E14.14.0.34", {"start": v(50.8, 11.5) * mm, "end": v(50.81, 11.5) * mm});
            skLineSegment(sketch, "E14.14.0.35", {"start": v(53.8, 11.5) * mm, "end": v(53.81, 11.5) * mm});
            skLineSegment(sketch, "E14.14.0.36", {"start": v(55.8, 8.5) * mm, "end": v(55.81, 8.5) * mm});
            skLineSegment(sketch, "E14.14.0.37", {"start": v(56.8, 8.5) * mm, "end": v(56.81, 8.5) * mm});
            skLineSegment(sketch, "E14.14.0.38", {"start": v(53.8, 8.5) * mm, "end": v(53.81, 8.5) * mm});
            skLineSegment(sketch, "E14.14.0.39", {"start": v(51.8, 8.5) * mm, "end": v(51.81, 8.5) * mm});
            skLineSegment(sketch, "E14.14.0.40", {"start": v(50.8, 8.5) * mm, "end": v(50.81, 8.5) * mm});
            skLineSegment(sketch, "E14.15.0.0", {"start": v(59.82, 11.5) * mm, "end": v(59.82, 6.5) * mm});
            skLineSegment(sketch, "E14.15.0.1", {"start": v(66.81, 11.5) * mm, "end": v(66.81, 8.5) * mm});
            skLineSegment(sketch, "E14.15.0.2", {"start": v(61.81, 11.5) * mm, "end": v(61.81, 8.5) * mm});
            skLineSegment(sketch, "E14.15.0.3", {"start": v(59.8, 11.5) * mm, "end": v(59.8, 6.5) * mm});
            skLineSegment(sketch, "E14.15.0.4", {"start": v(63.81, 11.5) * mm, "end": v(63.81, 8.5) * mm});
            skLineSegment(sketch, "E14.15.0.5", {"start": v(68.81, 11.5) * mm, "end": v(68.81, 8.5) * mm});
            skLineSegment(sketch, "E14.15.0.6", {"start": v(65.81, 11.5) * mm, "end": v(65.81, 8.5) * mm});
            skLineSegment(sketch, "E14.15.0.7", {"start": v(64.81, 11.5) * mm, "end": v(64.81, 8) * mm});
            skLineSegment(sketch, "E14.15.0.8", {"start": v(62.8, 11.5) * mm, "end": v(62.8, 8.5) * mm});
            skLineSegment(sketch, "E14.15.0.9", {"start": v(67.8, 11.5) * mm, "end": v(67.8, 8.5) * mm});
            skLineSegment(sketch, "E14.15.0.10", {"start": v(60.81, 11.5) * mm, "end": v(60.81, 8.5) * mm});
            skLineSegment(sketch, "E14.15.0.11", {"start": v(68.8, 11.5) * mm, "end": v(68.8, 8.5) * mm});
            skLineSegment(sketch, "E14.15.0.12", {"start": v(60.8, 8.5) * mm, "end": v(61.8, 8.5) * mm, "construction": true});
            skLineSegment(sketch, "E14.15.0.13", {"start": v(62.81, 11.5) * mm, "end": v(62.81, 8.5) * mm});
            skLineSegment(sketch, "E14.15.0.14", {"start": v(66.8, 11.5) * mm, "end": v(66.8, 8.5) * mm});
            skLineSegment(sketch, "E14.15.0.15", {"start": v(60.8, 11.5) * mm, "end": v(60.8, 8.5) * mm});
            skLineSegment(sketch, "E14.15.0.16", {"start": v(61.8, 11.5) * mm, "end": v(61.8, 8.5) * mm});
            skLineSegment(sketch, "E14.15.0.17", {"start": v(63.8, 11.5) * mm, "end": v(63.8, 8.5) * mm});
            skLineSegment(sketch, "E14.15.0.18", {"start": v(65.8, 11.5) * mm, "end": v(65.8, 8.5) * mm});
            skLineSegment(sketch, "E14.15.0.19", {"start": v(67.81, 11.5) * mm, "end": v(67.81, 8.5) * mm});
            skLineSegment(sketch, "E14.15.0.20", {"start": v(64.8, 11.5) * mm, "end": v(64.8, 8) * mm});
            skLineSegment(sketch, "E14.15.0.21", {"start": v(68.8, 8.5) * mm, "end": v(68.81, 8.5) * mm});
            skLineSegment(sketch, "E14.15.0.22", {"start": v(59.8, 11.5) * mm, "end": v(59.82, 11.5) * mm});
            skLineSegment(sketch, "E14.15.0.23", {"start": v(59.8, 6.5) * mm, "end": v(59.82, 6.5) * mm});
            skLineSegment(sketch, "E14.15.0.24", {"start": v(68.8, 11.5) * mm, "end": v(68.81, 11.5) * mm});
            skLineSegment(sketch, "E14.15.0.25", {"start": v(62.8, 11.5) * mm, "end": v(62.81, 11.5) * mm});
            skLineSegment(sketch, "E14.15.0.26", {"start": v(65.8, 11.5) * mm, "end": v(65.81, 11.5) * mm});
            skLineSegment(sketch, "E14.15.0.27", {"start": v(67.8, 8.5) * mm, "end": v(67.81, 8.5) * mm});
            skLineSegment(sketch, "E14.15.0.28", {"start": v(64.8, 8) * mm, "end": v(64.81, 8) * mm});
            skLineSegment(sketch, "E14.15.0.29", {"start": v(62.8, 8.5) * mm, "end": v(62.81, 8.5) * mm});
            skLineSegment(sketch, "E14.15.0.30", {"start": v(66.8, 11.5) * mm, "end": v(66.81, 11.5) * mm});
            skLineSegment(sketch, "E14.15.0.31", {"start": v(61.8, 11.5) * mm, "end": v(61.81, 11.5) * mm});
            skLineSegment(sketch, "E14.15.0.32", {"start": v(64.8, 11.5) * mm, "end": v(64.81, 11.5) * mm});
            skLineSegment(sketch, "E14.15.0.33", {"start": v(67.8, 11.5) * mm, "end": v(67.81, 11.5) * mm});
            skLineSegment(sketch, "E14.15.0.34", {"start": v(60.8, 11.5) * mm, "end": v(60.81, 11.5) * mm});
            skLineSegment(sketch, "E14.15.0.35", {"start": v(63.8, 11.5) * mm, "end": v(63.81, 11.5) * mm});
            skLineSegment(sketch, "E14.15.0.36", {"start": v(65.8, 8.5) * mm, "end": v(65.81, 8.5) * mm});
            skLineSegment(sketch, "E14.15.0.37", {"start": v(66.8, 8.5) * mm, "end": v(66.81, 8.5) * mm});
            skLineSegment(sketch, "E14.15.0.38", {"start": v(63.8, 8.5) * mm, "end": v(63.81, 8.5) * mm});
            skLineSegment(sketch, "E14.15.0.39", {"start": v(61.8, 8.5) * mm, "end": v(61.81, 8.5) * mm});
            skLineSegment(sketch, "E14.15.0.40", {"start": v(60.8, 8.5) * mm, "end": v(60.81, 8.5) * mm});
            skLineSegment(sketch, "E14.16.0.0", {"start": v(69.82, 11.5) * mm, "end": v(69.82, 6.5) * mm});
            skLineSegment(sketch, "E14.16.0.1", {"start": v(76.81, 11.5) * mm, "end": v(76.81, 8.5) * mm});
            skLineSegment(sketch, "E14.16.0.2", {"start": v(71.81, 11.5) * mm, "end": v(71.81, 8.5) * mm});
            skLineSegment(sketch, "E14.16.0.3", {"start": v(69.8, 11.5) * mm, "end": v(69.8, 6.5) * mm});
            skLineSegment(sketch, "E14.16.0.4", {"start": v(73.81, 11.5) * mm, "end": v(73.81, 8.5) * mm});
            skLineSegment(sketch, "E14.16.0.5", {"start": v(78.81, 11.5) * mm, "end": v(78.81, 8.5) * mm});
            skLineSegment(sketch, "E14.16.0.6", {"start": v(75.81, 11.5) * mm, "end": v(75.81, 8.5) * mm});
            skLineSegment(sketch, "E14.16.0.7", {"start": v(74.81, 11.5) * mm, "end": v(74.81, 8) * mm});
            skLineSegment(sketch, "E14.16.0.8", {"start": v(72.8, 11.5) * mm, "end": v(72.8, 8.5) * mm});
            skLineSegment(sketch, "E14.16.0.9", {"start": v(77.8, 11.5) * mm, "end": v(77.8, 8.5) * mm});
            skLineSegment(sketch, "E14.16.0.10", {"start": v(70.81, 11.5) * mm, "end": v(70.81, 8.5) * mm});
            skLineSegment(sketch, "E14.16.0.11", {"start": v(78.8, 11.5) * mm, "end": v(78.8, 8.5) * mm});
            skLineSegment(sketch, "E14.16.0.12", {"start": v(70.8, 8.5) * mm, "end": v(71.8, 8.5) * mm, "construction": true});
            skLineSegment(sketch, "E14.16.0.13", {"start": v(72.81, 11.5) * mm, "end": v(72.81, 8.5) * mm});
            skLineSegment(sketch, "E14.16.0.14", {"start": v(76.8, 11.5) * mm, "end": v(76.8, 8.5) * mm});
            skLineSegment(sketch, "E14.16.0.15", {"start": v(70.8, 11.5) * mm, "end": v(70.8, 8.5) * mm});
            skLineSegment(sketch, "E14.16.0.16", {"start": v(71.8, 11.5) * mm, "end": v(71.8, 8.5) * mm});
            skLineSegment(sketch, "E14.16.0.17", {"start": v(73.8, 11.5) * mm, "end": v(73.8, 8.5) * mm});
            skLineSegment(sketch, "E14.16.0.18", {"start": v(75.8, 11.5) * mm, "end": v(75.8, 8.5) * mm});
            skLineSegment(sketch, "E14.16.0.19", {"start": v(77.81, 11.5) * mm, "end": v(77.81, 8.5) * mm});
            skLineSegment(sketch, "E14.16.0.20", {"start": v(74.8, 11.5) * mm, "end": v(74.8, 8) * mm});
            skLineSegment(sketch, "E14.16.0.21", {"start": v(78.8, 8.5) * mm, "end": v(78.81, 8.5) * mm});
            skLineSegment(sketch, "E14.16.0.22", {"start": v(69.8, 11.5) * mm, "end": v(69.82, 11.5) * mm});
            skLineSegment(sketch, "E14.16.0.23", {"start": v(69.8, 6.5) * mm, "end": v(69.82, 6.5) * mm});
            skLineSegment(sketch, "E14.16.0.24", {"start": v(78.8, 11.5) * mm, "end": v(78.81, 11.5) * mm});
            skLineSegment(sketch, "E14.16.0.25", {"start": v(72.8, 11.5) * mm, "end": v(72.81, 11.5) * mm});
            skLineSegment(sketch, "E14.16.0.26", {"start": v(75.8, 11.5) * mm, "end": v(75.81, 11.5) * mm});
            skLineSegment(sketch, "E14.16.0.27", {"start": v(77.8, 8.5) * mm, "end": v(77.81, 8.5) * mm});
            skLineSegment(sketch, "E14.16.0.28", {"start": v(74.8, 8) * mm, "end": v(74.81, 8) * mm});
            skLineSegment(sketch, "E14.16.0.29", {"start": v(72.8, 8.5) * mm, "end": v(72.81, 8.5) * mm});
            skLineSegment(sketch, "E14.16.0.30", {"start": v(76.8, 11.5) * mm, "end": v(76.81, 11.5) * mm});
            skLineSegment(sketch, "E14.16.0.31", {"start": v(71.8, 11.5) * mm, "end": v(71.81, 11.5) * mm});
            skLineSegment(sketch, "E14.16.0.32", {"start": v(74.8, 11.5) * mm, "end": v(74.81, 11.5) * mm});
            skLineSegment(sketch, "E14.16.0.33", {"start": v(77.8, 11.5) * mm, "end": v(77.81, 11.5) * mm});
            skLineSegment(sketch, "E14.16.0.34", {"start": v(70.8, 11.5) * mm, "end": v(70.81, 11.5) * mm});
            skLineSegment(sketch, "E14.16.0.35", {"start": v(73.8, 11.5) * mm, "end": v(73.81, 11.5) * mm});
            skLineSegment(sketch, "E14.16.0.36", {"start": v(75.8, 8.5) * mm, "end": v(75.81, 8.5) * mm});
            skLineSegment(sketch, "E14.16.0.37", {"start": v(76.8, 8.5) * mm, "end": v(76.81, 8.5) * mm});
            skLineSegment(sketch, "E14.16.0.38", {"start": v(73.8, 8.5) * mm, "end": v(73.81, 8.5) * mm});
            skLineSegment(sketch, "E14.16.0.39", {"start": v(71.8, 8.5) * mm, "end": v(71.81, 8.5) * mm});
            skLineSegment(sketch, "E14.16.0.40", {"start": v(70.8, 8.5) * mm, "end": v(70.81, 8.5) * mm});
            skLineSegment(sketch, "E14.17.0.0", {"start": v(79.82, 11.5) * mm, "end": v(79.82, 6.5) * mm});
            skLineSegment(sketch, "E14.17.0.1", {"start": v(86.81, 11.5) * mm, "end": v(86.81, 8.5) * mm});
            skLineSegment(sketch, "E14.17.0.2", {"start": v(81.81, 11.5) * mm, "end": v(81.81, 8.5) * mm});
            skLineSegment(sketch, "E14.17.0.3", {"start": v(79.8, 11.5) * mm, "end": v(79.8, 6.5) * mm});
            skLineSegment(sketch, "E14.17.0.4", {"start": v(83.81, 11.5) * mm, "end": v(83.81, 8.5) * mm});
            skLineSegment(sketch, "E14.17.0.5", {"start": v(88.81, 11.5) * mm, "end": v(88.81, 8.5) * mm});
            skLineSegment(sketch, "E14.17.0.6", {"start": v(85.81, 11.5) * mm, "end": v(85.81, 8.5) * mm});
            skLineSegment(sketch, "E14.17.0.7", {"start": v(84.81, 11.5) * mm, "end": v(84.81, 8) * mm});
            skLineSegment(sketch, "E14.17.0.8", {"start": v(82.8, 11.5) * mm, "end": v(82.8, 8.5) * mm});
            skLineSegment(sketch, "E14.17.0.9", {"start": v(87.8, 11.5) * mm, "end": v(87.8, 8.5) * mm});
            skLineSegment(sketch, "E14.17.0.10", {"start": v(80.81, 11.5) * mm, "end": v(80.81, 8.5) * mm});
            skLineSegment(sketch, "E14.17.0.11", {"start": v(88.8, 11.5) * mm, "end": v(88.8, 8.5) * mm});
            skLineSegment(sketch, "E14.17.0.12", {"start": v(80.8, 8.5) * mm, "end": v(81.8, 8.5) * mm, "construction": true});
            skLineSegment(sketch, "E14.17.0.13", {"start": v(82.81, 11.5) * mm, "end": v(82.81, 8.5) * mm});
            skLineSegment(sketch, "E14.17.0.14", {"start": v(86.8, 11.5) * mm, "end": v(86.8, 8.5) * mm});
            skLineSegment(sketch, "E14.17.0.15", {"start": v(80.8, 11.5) * mm, "end": v(80.8, 8.5) * mm});
            skLineSegment(sketch, "E14.17.0.16", {"start": v(81.8, 11.5) * mm, "end": v(81.8, 8.5) * mm});
            skLineSegment(sketch, "E14.17.0.17", {"start": v(83.8, 11.5) * mm, "end": v(83.8, 8.5) * mm});
            skLineSegment(sketch, "E14.17.0.18", {"start": v(85.8, 11.5) * mm, "end": v(85.8, 8.5) * mm});
            skLineSegment(sketch, "E14.17.0.19", {"start": v(87.81, 11.5) * mm, "end": v(87.81, 8.5) * mm});
            skLineSegment(sketch, "E14.17.0.20", {"start": v(84.8, 11.5) * mm, "end": v(84.8, 8) * mm});
            skLineSegment(sketch, "E14.17.0.21", {"start": v(88.8, 8.5) * mm, "end": v(88.81, 8.5) * mm});
            skLineSegment(sketch, "E14.17.0.22", {"start": v(79.8, 11.5) * mm, "end": v(79.82, 11.5) * mm});
            skLineSegment(sketch, "E14.17.0.23", {"start": v(79.8, 6.5) * mm, "end": v(79.82, 6.5) * mm});
            skLineSegment(sketch, "E14.17.0.24", {"start": v(88.8, 11.5) * mm, "end": v(88.81, 11.5) * mm});
            skLineSegment(sketch, "E14.17.0.25", {"start": v(82.8, 11.5) * mm, "end": v(82.81, 11.5) * mm});
            skLineSegment(sketch, "E14.17.0.26", {"start": v(85.8, 11.5) * mm, "end": v(85.81, 11.5) * mm});
            skLineSegment(sketch, "E14.17.0.27", {"start": v(87.8, 8.5) * mm, "end": v(87.81, 8.5) * mm});
            skLineSegment(sketch, "E14.17.0.28", {"start": v(84.8, 8) * mm, "end": v(84.81, 8) * mm});
            skLineSegment(sketch, "E14.17.0.29", {"start": v(82.8, 8.5) * mm, "end": v(82.81, 8.5) * mm});
            skLineSegment(sketch, "E14.17.0.30", {"start": v(86.8, 11.5) * mm, "end": v(86.81, 11.5) * mm});
            skLineSegment(sketch, "E14.17.0.31", {"start": v(81.8, 11.5) * mm, "end": v(81.81, 11.5) * mm});
            skLineSegment(sketch, "E14.17.0.32", {"start": v(84.8, 11.5) * mm, "end": v(84.81, 11.5) * mm});
            skLineSegment(sketch, "E14.17.0.33", {"start": v(87.8, 11.5) * mm, "end": v(87.81, 11.5) * mm});
            skLineSegment(sketch, "E14.17.0.34", {"start": v(80.8, 11.5) * mm, "end": v(80.81, 11.5) * mm});
            skLineSegment(sketch, "E14.17.0.35", {"start": v(83.8, 11.5) * mm, "end": v(83.81, 11.5) * mm});
            skLineSegment(sketch, "E14.17.0.36", {"start": v(85.8, 8.5) * mm, "end": v(85.81, 8.5) * mm});
            skLineSegment(sketch, "E14.17.0.37", {"start": v(86.8, 8.5) * mm, "end": v(86.81, 8.5) * mm});
            skLineSegment(sketch, "E14.17.0.38", {"start": v(83.8, 8.5) * mm, "end": v(83.81, 8.5) * mm});
            skLineSegment(sketch, "E14.17.0.39", {"start": v(81.8, 8.5) * mm, "end": v(81.81, 8.5) * mm});
            skLineSegment(sketch, "E14.17.0.40", {"start": v(80.8, 8.5) * mm, "end": v(80.81, 8.5) * mm});
            skLineSegment(sketch, "E14.18.0.0", {"start": v(89.82, 11.5) * mm, "end": v(89.82, 6.5) * mm});
            skLineSegment(sketch, "E14.18.0.1", {"start": v(96.81, 11.5) * mm, "end": v(96.81, 8.5) * mm});
            skLineSegment(sketch, "E14.18.0.2", {"start": v(91.81, 11.5) * mm, "end": v(91.81, 8.5) * mm});
            skLineSegment(sketch, "E14.18.0.3", {"start": v(89.8, 11.5) * mm, "end": v(89.8, 6.5) * mm});
            skLineSegment(sketch, "E14.18.0.4", {"start": v(93.81, 11.5) * mm, "end": v(93.81, 8.5) * mm});
            skLineSegment(sketch, "E14.18.0.5", {"start": v(98.81, 11.5) * mm, "end": v(98.81, 8.5) * mm});
            skLineSegment(sketch, "E14.18.0.6", {"start": v(95.81, 11.5) * mm, "end": v(95.81, 8.5) * mm});
            skLineSegment(sketch, "E14.18.0.7", {"start": v(94.81, 11.5) * mm, "end": v(94.81, 8) * mm});
            skLineSegment(sketch, "E14.18.0.8", {"start": v(92.8, 11.5) * mm, "end": v(92.8, 8.5) * mm});
            skLineSegment(sketch, "E14.18.0.9", {"start": v(97.8, 11.5) * mm, "end": v(97.8, 8.5) * mm});
            skLineSegment(sketch, "E14.18.0.10", {"start": v(90.81, 11.5) * mm, "end": v(90.81, 8.5) * mm});
            skLineSegment(sketch, "E14.18.0.11", {"start": v(98.8, 11.5) * mm, "end": v(98.8, 8.5) * mm});
            skLineSegment(sketch, "E14.18.0.12", {"start": v(90.8, 8.5) * mm, "end": v(91.8, 8.5) * mm, "construction": true});
            skLineSegment(sketch, "E14.18.0.13", {"start": v(92.81, 11.5) * mm, "end": v(92.81, 8.5) * mm});
            skLineSegment(sketch, "E14.18.0.14", {"start": v(96.8, 11.5) * mm, "end": v(96.8, 8.5) * mm});
            skLineSegment(sketch, "E14.18.0.15", {"start": v(90.8, 11.5) * mm, "end": v(90.8, 8.5) * mm});
            skLineSegment(sketch, "E14.18.0.16", {"start": v(91.8, 11.5) * mm, "end": v(91.8, 8.5) * mm});
            skLineSegment(sketch, "E14.18.0.17", {"start": v(93.8, 11.5) * mm, "end": v(93.8, 8.5) * mm});
            skLineSegment(sketch, "E14.18.0.18", {"start": v(95.8, 11.5) * mm, "end": v(95.8, 8.5) * mm});
            skLineSegment(sketch, "E14.18.0.19", {"start": v(97.81, 11.5) * mm, "end": v(97.81, 8.5) * mm});
            skLineSegment(sketch, "E14.18.0.20", {"start": v(94.8, 11.5) * mm, "end": v(94.8, 8) * mm});
            skLineSegment(sketch, "E14.18.0.21", {"start": v(98.8, 8.5) * mm, "end": v(98.81, 8.5) * mm});
            skLineSegment(sketch, "E14.18.0.22", {"start": v(89.8, 11.5) * mm, "end": v(89.82, 11.5) * mm});
            skLineSegment(sketch, "E14.18.0.23", {"start": v(89.8, 6.5) * mm, "end": v(89.82, 6.5) * mm});
            skLineSegment(sketch, "E14.18.0.24", {"start": v(98.8, 11.5) * mm, "end": v(98.81, 11.5) * mm});
            skLineSegment(sketch, "E14.18.0.25", {"start": v(92.8, 11.5) * mm, "end": v(92.81, 11.5) * mm});
            skLineSegment(sketch, "E14.18.0.26", {"start": v(95.8, 11.5) * mm, "end": v(95.81, 11.5) * mm});
            skLineSegment(sketch, "E14.18.0.27", {"start": v(97.8, 8.5) * mm, "end": v(97.81, 8.5) * mm});
            skLineSegment(sketch, "E14.18.0.28", {"start": v(94.8, 8) * mm, "end": v(94.81, 8) * mm});
            skLineSegment(sketch, "E14.18.0.29", {"start": v(92.8, 8.5) * mm, "end": v(92.81, 8.5) * mm});
            skLineSegment(sketch, "E14.18.0.30", {"start": v(96.8, 11.5) * mm, "end": v(96.81, 11.5) * mm});
            skLineSegment(sketch, "E14.18.0.31", {"start": v(91.8, 11.5) * mm, "end": v(91.81, 11.5) * mm});
            skLineSegment(sketch, "E14.18.0.32", {"start": v(94.8, 11.5) * mm, "end": v(94.81, 11.5) * mm});
            skLineSegment(sketch, "E14.18.0.33", {"start": v(97.8, 11.5) * mm, "end": v(97.81, 11.5) * mm});
            skLineSegment(sketch, "E14.18.0.34", {"start": v(90.8, 11.5) * mm, "end": v(90.81, 11.5) * mm});
            skLineSegment(sketch, "E14.18.0.35", {"start": v(93.8, 11.5) * mm, "end": v(93.81, 11.5) * mm});
            skLineSegment(sketch, "E14.18.0.36", {"start": v(95.8, 8.5) * mm, "end": v(95.81, 8.5) * mm});
            skLineSegment(sketch, "E14.18.0.37", {"start": v(96.8, 8.5) * mm, "end": v(96.81, 8.5) * mm});
            skLineSegment(sketch, "E14.18.0.38", {"start": v(93.8, 8.5) * mm, "end": v(93.81, 8.5) * mm});
            skLineSegment(sketch, "E14.18.0.39", {"start": v(91.8, 8.5) * mm, "end": v(91.81, 8.5) * mm});
            skLineSegment(sketch, "E14.18.0.40", {"start": v(90.8, 8.5) * mm, "end": v(90.81, 8.5) * mm});
            skLineSegment(sketch, "E14.19.0.0", {"start": v(99.82, 11.5) * mm, "end": v(99.82, 6.5) * mm});
            skLineSegment(sketch, "E14.19.0.1", {"start": v(106.81, 11.5) * mm, "end": v(106.81, 8.5) * mm});
            skLineSegment(sketch, "E14.19.0.2", {"start": v(101.81, 11.5) * mm, "end": v(101.81, 8.5) * mm});
            skLineSegment(sketch, "E14.19.0.3", {"start": v(99.8, 11.5) * mm, "end": v(99.8, 6.5) * mm});
            skLineSegment(sketch, "E14.19.0.4", {"start": v(103.81, 11.5) * mm, "end": v(103.81, 8.5) * mm});
            skLineSegment(sketch, "E14.19.0.5", {"start": v(108.81, 11.5) * mm, "end": v(108.81, 8.5) * mm});
            skLineSegment(sketch, "E14.19.0.6", {"start": v(105.81, 11.5) * mm, "end": v(105.81, 8.5) * mm});
            skLineSegment(sketch, "E14.19.0.7", {"start": v(104.81, 11.5) * mm, "end": v(104.81, 8) * mm});
            skLineSegment(sketch, "E14.19.0.8", {"start": v(102.8, 11.5) * mm, "end": v(102.8, 8.5) * mm});
            skLineSegment(sketch, "E14.19.0.9", {"start": v(107.8, 11.5) * mm, "end": v(107.8, 8.5) * mm});
            skLineSegment(sketch, "E14.19.0.10", {"start": v(100.81, 11.5) * mm, "end": v(100.81, 8.5) * mm});
            skLineSegment(sketch, "E14.19.0.11", {"start": v(108.8, 11.5) * mm, "end": v(108.8, 8.5) * mm});
            skLineSegment(sketch, "E14.19.0.12", {"start": v(100.8, 8.5) * mm, "end": v(101.8, 8.5) * mm, "construction": true});
            skLineSegment(sketch, "E14.19.0.13", {"start": v(102.81, 11.5) * mm, "end": v(102.81, 8.5) * mm});
            skLineSegment(sketch, "E14.19.0.14", {"start": v(106.8, 11.5) * mm, "end": v(106.8, 8.5) * mm});
            skLineSegment(sketch, "E14.19.0.15", {"start": v(100.8, 11.5) * mm, "end": v(100.8, 8.5) * mm});
            skLineSegment(sketch, "E14.19.0.16", {"start": v(101.8, 11.5) * mm, "end": v(101.8, 8.5) * mm});
            skLineSegment(sketch, "E14.19.0.17", {"start": v(103.8, 11.5) * mm, "end": v(103.8, 8.5) * mm});
            skLineSegment(sketch, "E14.19.0.18", {"start": v(105.8, 11.5) * mm, "end": v(105.8, 8.5) * mm});
            skLineSegment(sketch, "E14.19.0.19", {"start": v(107.81, 11.5) * mm, "end": v(107.81, 8.5) * mm});
            skLineSegment(sketch, "E14.19.0.20", {"start": v(104.8, 11.5) * mm, "end": v(104.8, 8) * mm});
            skLineSegment(sketch, "E14.19.0.21", {"start": v(108.8, 8.5) * mm, "end": v(108.81, 8.5) * mm});
            skLineSegment(sketch, "E14.19.0.22", {"start": v(99.8, 11.5) * mm, "end": v(99.82, 11.5) * mm});
            skLineSegment(sketch, "E14.19.0.23", {"start": v(99.8, 6.5) * mm, "end": v(99.82, 6.5) * mm});
            skLineSegment(sketch, "E14.19.0.24", {"start": v(108.8, 11.5) * mm, "end": v(108.81, 11.5) * mm});
            skLineSegment(sketch, "E14.19.0.25", {"start": v(102.8, 11.5) * mm, "end": v(102.81, 11.5) * mm});
            skLineSegment(sketch, "E14.19.0.26", {"start": v(105.8, 11.5) * mm, "end": v(105.81, 11.5) * mm});
            skLineSegment(sketch, "E14.19.0.27", {"start": v(107.8, 8.5) * mm, "end": v(107.81, 8.5) * mm});
            skLineSegment(sketch, "E14.19.0.28", {"start": v(104.8, 8) * mm, "end": v(104.81, 8) * mm});
            skLineSegment(sketch, "E14.19.0.29", {"start": v(102.8, 8.5) * mm, "end": v(102.81, 8.5) * mm});
            skLineSegment(sketch, "E14.19.0.30", {"start": v(106.8, 11.5) * mm, "end": v(106.81, 11.5) * mm});
            skLineSegment(sketch, "E14.19.0.31", {"start": v(101.8, 11.5) * mm, "end": v(101.81, 11.5) * mm});
            skLineSegment(sketch, "E14.19.0.32", {"start": v(104.8, 11.5) * mm, "end": v(104.81, 11.5) * mm});
            skLineSegment(sketch, "E14.19.0.33", {"start": v(107.8, 11.5) * mm, "end": v(107.81, 11.5) * mm});
            skLineSegment(sketch, "E14.19.0.34", {"start": v(100.8, 11.5) * mm, "end": v(100.81, 11.5) * mm});
            skLineSegment(sketch, "E14.19.0.35", {"start": v(103.8, 11.5) * mm, "end": v(103.81, 11.5) * mm});
            skLineSegment(sketch, "E14.19.0.36", {"start": v(105.8, 8.5) * mm, "end": v(105.81, 8.5) * mm});
            skLineSegment(sketch, "E14.19.0.37", {"start": v(106.8, 8.5) * mm, "end": v(106.81, 8.5) * mm});
            skLineSegment(sketch, "E14.19.0.38", {"start": v(103.8, 8.5) * mm, "end": v(103.81, 8.5) * mm});
            skLineSegment(sketch, "E14.19.0.39", {"start": v(101.8, 8.5) * mm, "end": v(101.81, 8.5) * mm});
            skLineSegment(sketch, "E14.19.0.40", {"start": v(100.8, 8.5) * mm, "end": v(100.81, 8.5) * mm});
            skLineSegment(sketch, "E14.direction1", {"start": v(-90.2, 6.5) * mm, "end": v(-80.2, 6.5) * mm, "construction": true});
            skText(sketch, "E15", { "text": "1", "fontName": "OpenSans-Regular.ttf"});
            skLineSegment(sketch, "E16", {"start": v(-80.8, 5.46) * mm, "end": v(110.84, 5.46) * mm, "construction": true});
            skLineSegment(sketch, "E17", {"start": v(-80.8, 3.58) * mm, "end": v(111.99, 3.58) * mm, "construction": true});
            skText(sketch, "E18", { "text": "2", "fontName": "OpenSans-Regular.ttf"});
            skText(sketch, "E19", { "text": "3", "fontName": "OpenSans-Regular.ttf"});
            skText(sketch, "E20", { "text": "4", "fontName": "OpenSans-Regular.ttf"});
            skText(sketch, "E21", { "text": "5", "fontName": "OpenSans-Regular.ttf"});
            skText(sketch, "E22", { "text": "6", "fontName": "OpenSans-Regular.ttf"});
            skText(sketch, "E23", { "text": "7", "fontName": "OpenSans-Regular.ttf"});
            skText(sketch, "E24", { "text": "8", "fontName": "OpenSans-Regular.ttf"});
            skText(sketch, "E25", { "text": "9", "fontName": "OpenSans-Regular.ttf"});
            skText(sketch, "E26", { "text": "10", "fontName": "OpenSans-Regular.ttf"});
            const initialGuessF2  = {"E15": [-0.0808, 0.00358, 1, 0, 0.00188], "E18": [-0.07066, 0.00358, 1, 0, 0.00188], "E19": [-0.06055, 0.00358, 1, 0, 0.00188], "E20": [-0.05069, 0.00358, 1, 0, 0.00188], "E21": [-0.04074, 0.00358, 1, 0, 0.00188], "E22": [-0.03068, 0.00358, 1, 0, 0.00188], "E23": [-0.02093, 0.00358, 1, 0, 0.00188], "E24": [-0.01073, 0.00358, 1, 0, 0.00188], "E25": [-0.0008, 0.00358, 1, 0, 0.00188], "E26": [0.00916, 0.00358, 1, 0, 0.00188]};
            skSetInitialGuess(sketch, initialGuessF2);
            skSolve(sketch);
        }
        {
            var Q0;
            Q0 = qSketchRegion(id + "F2", true);
            extrude(context, id + "F3", {"entities" : qUnion([Q0]), "operationType" : NewBodyOperationType.REMOVE, "oppositeDirection" : true, "depth" : 0.1 * mm});
        }
    });
